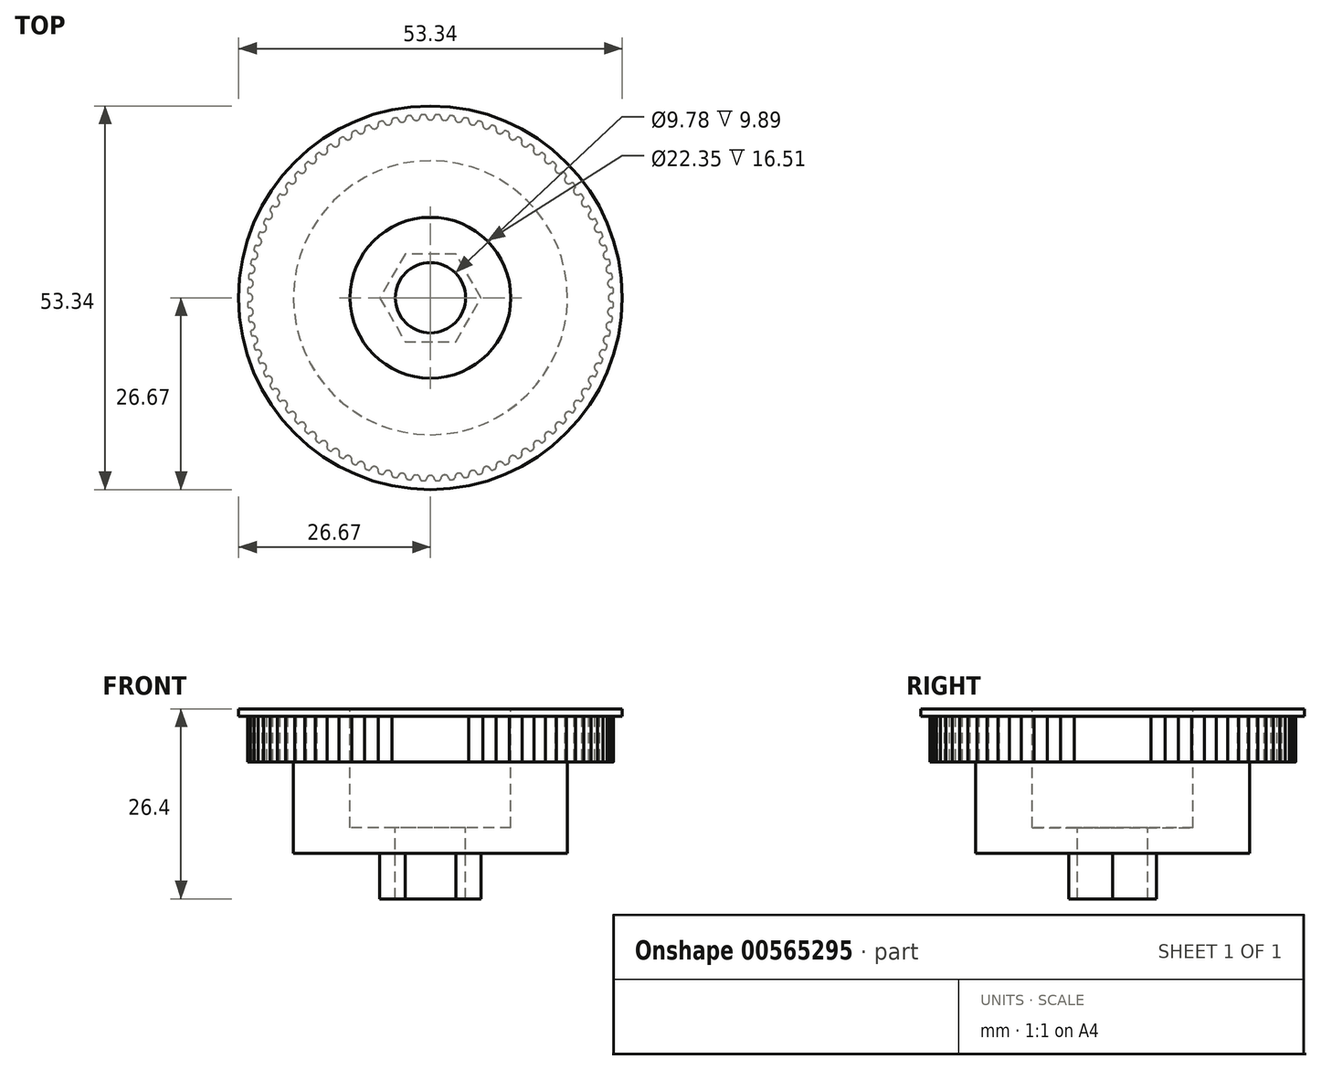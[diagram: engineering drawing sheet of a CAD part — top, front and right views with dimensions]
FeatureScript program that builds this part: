
annotation { "Feature Type Name" : "Feature", "Feature Type Description" : "" }
export const myFeature = defineFeature(function(context is Context, id is Id, definition is map)
    precondition{}
    {
        {
            var Q0;
            Q0=qCreatedBy(makeId("Top.planeOp"),FACE);
            var sketch = newSketch(context, id + "F0", { "sketchPlane" : qUnion([Q0])});
            skArc(sketch, "E0", {"start": v(0, 24.71) * mm, "mid": v(0.3, 24.8) * mm, "end": v(0.5, 25.03) * mm});
            skArc(sketch, "E1", {"start": v(0.5, 25.03) * mm, "mid": v(0.54, 25.14) * mm, "end": v(0.58, 25.25) * mm});
            skArc(sketch, "E2", {"start": v(1.46, 25) * mm, "mid": v(1.65, 24.75) * mm, "end": v(1.94, 24.64) * mm});
            skArc(sketch, "E3", {"start": v(1.4, 25.22) * mm, "mid": v(1.43, 25.1) * mm, "end": v(1.46, 25) * mm});
            skArc(sketch, "E4.trimOffspring", {"start": v(1.17, 25.44) * mm, "mid": v(1, 25.44) * mm, "end": v(0.83, 25.45) * mm});
            skPoint(sketch, "E5.visualSharp", {"position": v(0.6, 25.46) * mm});
            skArc(sketch, "E5.filletArc", {"start": v(0.83, 25.45) * mm, "mid": v(0.67, 25.4) * mm, "end": v(0.58, 25.25) * mm});
            skPoint(sketch, "E6.visualSharp", {"position": v(1.4, 25.42) * mm});
            skArc(sketch, "E6.filletArc", {"start": v(1.4, 25.22) * mm, "mid": v(1.33, 25.37) * mm, "end": v(1.17, 25.44) * mm});
            skArc(sketch, "E7.1.0", {"start": v(-1.94, 24.64) * mm, "mid": v(-1.65, 24.75) * mm, "end": v(-1.46, 25) * mm});
            skArc(sketch, "E7.1.1", {"start": v(-1.46, 25) * mm, "mid": v(-1.43, 25.1) * mm, "end": v(-1.4, 25.22) * mm});
            skArc(sketch, "E7.1.2", {"start": v(-1.17, 25.44) * mm, "mid": v(-1.33, 25.37) * mm, "end": v(-1.4, 25.22) * mm});
            skArc(sketch, "E7.1.3", {"start": v(-0.83, 25.45) * mm, "mid": v(-1, 25.44) * mm, "end": v(-1.17, 25.44) * mm});
            skArc(sketch, "E7.1.4", {"start": v(-0.58, 25.25) * mm, "mid": v(-0.67, 25.4) * mm, "end": v(-0.83, 25.45) * mm});
            skArc(sketch, "E7.1.5", {"start": v(-0.58, 25.25) * mm, "mid": v(-0.54, 25.14) * mm, "end": v(-0.5, 25.03) * mm});
            skArc(sketch, "E7.1.6", {"start": v(-0.5, 25.03) * mm, "mid": v(-0.3, 24.8) * mm, "end": v(0, 24.71) * mm});
            skArc(sketch, "E7.2.0", {"start": v(-3.87, 24.4) * mm, "mid": v(-3.59, 24.54) * mm, "end": v(-3.42, 24.8) * mm});
            skArc(sketch, "E7.2.1", {"start": v(-3.42, 24.8) * mm, "mid": v(-3.4, 24.91) * mm, "end": v(-3.38, 25.03) * mm});
            skArc(sketch, "E7.2.2", {"start": v(-3.16, 25.27) * mm, "mid": v(-3.31, 25.19) * mm, "end": v(-3.38, 25.03) * mm});
            skArc(sketch, "E7.2.3", {"start": v(-2.83, 25.3) * mm, "mid": v(-3, 25.29) * mm, "end": v(-3.16, 25.27) * mm});
            skArc(sketch, "E7.2.4", {"start": v(-2.55, 25.13) * mm, "mid": v(-2.66, 25.27) * mm, "end": v(-2.83, 25.3) * mm});
            skArc(sketch, "E7.2.5", {"start": v(-2.55, 25.13) * mm, "mid": v(-2.52, 25.02) * mm, "end": v(-2.46, 24.91) * mm});
            skArc(sketch, "E7.2.6", {"start": v(-2.46, 24.91) * mm, "mid": v(-2.24, 24.7) * mm, "end": v(-1.94, 24.64) * mm});
            skArc(sketch, "E7.3.0", {"start": v(-5.77, 24.03) * mm, "mid": v(-5.5, 24.18) * mm, "end": v(-5.36, 24.46) * mm});
            skArc(sketch, "E7.3.1", {"start": v(-5.36, 24.46) * mm, "mid": v(-5.34, 24.57) * mm, "end": v(-5.33, 24.69) * mm});
            skArc(sketch, "E7.3.2", {"start": v(-5.13, 24.94) * mm, "mid": v(-5.28, 24.85) * mm, "end": v(-5.33, 24.69) * mm});
            skArc(sketch, "E7.3.3", {"start": v(-4.8, 25) * mm, "mid": v(-4.97, 24.97) * mm, "end": v(-5.13, 24.94) * mm});
            skArc(sketch, "E7.3.4", {"start": v(-4.52, 24.85) * mm, "mid": v(-4.63, 24.98) * mm, "end": v(-4.8, 25) * mm});
            skArc(sketch, "E7.3.5", {"start": v(-4.52, 24.85) * mm, "mid": v(-4.47, 24.74) * mm, "end": v(-4.41, 24.64) * mm});
            skArc(sketch, "E7.3.6", {"start": v(-4.41, 24.64) * mm, "mid": v(-4.17, 24.45) * mm, "end": v(-3.87, 24.4) * mm});
            skArc(sketch, "E7.4.0", {"start": v(-7.64, 23.5) * mm, "mid": v(-7.38, 23.68) * mm, "end": v(-7.26, 23.96) * mm});
            skArc(sketch, "E7.4.1", {"start": v(-7.26, 23.96) * mm, "mid": v(-7.25, 24.08) * mm, "end": v(-7.26, 24.2) * mm});
            skArc(sketch, "E7.4.2", {"start": v(-7.07, 24.46) * mm, "mid": v(-7.21, 24.36) * mm, "end": v(-7.26, 24.2) * mm});
            skArc(sketch, "E7.4.3", {"start": v(-6.75, 24.55) * mm, "mid": v(-6.91, 24.5) * mm, "end": v(-7.07, 24.46) * mm});
            skArc(sketch, "E7.4.4", {"start": v(-6.45, 24.42) * mm, "mid": v(-6.58, 24.54) * mm, "end": v(-6.75, 24.55) * mm});
            skArc(sketch, "E7.4.5", {"start": v(-6.45, 24.42) * mm, "mid": v(-6.4, 24.32) * mm, "end": v(-6.33, 24.22) * mm});
            skArc(sketch, "E7.4.6", {"start": v(-6.33, 24.22) * mm, "mid": v(-6.08, 24.05) * mm, "end": v(-5.77, 24.03) * mm});
            skArc(sketch, "E7.5.0", {"start": v(-9.46, 22.83) * mm, "mid": v(-9.22, 23.03) * mm, "end": v(-9.12, 23.32) * mm});
            skArc(sketch, "E7.5.1", {"start": v(-9.12, 23.32) * mm, "mid": v(-9.12, 23.43) * mm, "end": v(-9.13, 23.55) * mm});
            skArc(sketch, "E7.5.2", {"start": v(-8.97, 23.83) * mm, "mid": v(-9.1, 23.72) * mm, "end": v(-9.13, 23.55) * mm});
            skArc(sketch, "E7.5.3", {"start": v(-8.66, 23.95) * mm, "mid": v(-8.81, 23.89) * mm, "end": v(-8.97, 23.83) * mm});
            skArc(sketch, "E7.5.4", {"start": v(-8.35, 23.84) * mm, "mid": v(-8.48, 23.95) * mm, "end": v(-8.66, 23.95) * mm});
            skArc(sketch, "E7.5.5", {"start": v(-8.35, 23.84) * mm, "mid": v(-8.29, 23.74) * mm, "end": v(-8.21, 23.65) * mm});
            skArc(sketch, "E7.5.6", {"start": v(-8.21, 23.65) * mm, "mid": v(-7.95, 23.5) * mm, "end": v(-7.64, 23.5) * mm});
            skArc(sketch, "E7.6.0", {"start": v(-11.22, 22.02) * mm, "mid": v(-11, 22.23) * mm, "end": v(-10.92, 22.53) * mm});
            skArc(sketch, "E7.6.1", {"start": v(-10.92, 22.53) * mm, "mid": v(-10.93, 22.65) * mm, "end": v(-10.95, 22.76) * mm});
            skArc(sketch, "E7.6.2", {"start": v(-10.81, 23.05) * mm, "mid": v(-10.93, 22.93) * mm, "end": v(-10.95, 22.76) * mm});
            skArc(sketch, "E7.6.3", {"start": v(-10.5, 23.2) * mm, "mid": v(-10.66, 23.12) * mm, "end": v(-10.81, 23.05) * mm});
            skArc(sketch, "E7.6.4", {"start": v(-10.2, 23.1) * mm, "mid": v(-10.34, 23.2) * mm, "end": v(-10.5, 23.2) * mm});
            skArc(sketch, "E7.6.5", {"start": v(-10.2, 23.1) * mm, "mid": v(-10.12, 23.02) * mm, "end": v(-10.04, 22.93) * mm});
            skArc(sketch, "E7.6.6", {"start": v(-10.04, 22.93) * mm, "mid": v(-9.76, 22.8) * mm, "end": v(-9.46, 22.83) * mm});
            skArc(sketch, "E7.7.0", {"start": v(-12.91, 21.07) * mm, "mid": v(-12.7, 21.3) * mm, "end": v(-12.65, 21.6) * mm});
            skArc(sketch, "E7.7.1", {"start": v(-12.65, 21.6) * mm, "mid": v(-12.67, 21.72) * mm, "end": v(-12.7, 21.83) * mm});
            skArc(sketch, "E7.7.2", {"start": v(-12.59, 22.13) * mm, "mid": v(-12.7, 22) * mm, "end": v(-12.7, 21.83) * mm});
            skArc(sketch, "E7.7.3", {"start": v(-12.3, 22.3) * mm, "mid": v(-12.44, 22.22) * mm, "end": v(-12.59, 22.13) * mm});
            skArc(sketch, "E7.7.4", {"start": v(-11.98, 22.24) * mm, "mid": v(-12.12, 22.33) * mm, "end": v(-12.3, 22.3) * mm});
            skArc(sketch, "E7.7.5", {"start": v(-11.98, 22.24) * mm, "mid": v(-11.9, 22.15) * mm, "end": v(-11.81, 22.08) * mm});
            skArc(sketch, "E7.7.6", {"start": v(-11.81, 22.08) * mm, "mid": v(-11.52, 21.96) * mm, "end": v(-11.22, 22.02) * mm});
            skArc(sketch, "E7.8.0", {"start": v(-14.53, 20) * mm, "mid": v(-14.34, 20.24) * mm, "end": v(-14.3, 20.54) * mm});
            skArc(sketch, "E7.8.1", {"start": v(-14.3, 20.54) * mm, "mid": v(-14.34, 20.66) * mm, "end": v(-14.38, 20.77) * mm});
            skArc(sketch, "E7.8.2", {"start": v(-14.29, 21.08) * mm, "mid": v(-14.39, 20.94) * mm, "end": v(-14.38, 20.77) * mm});
            skArc(sketch, "E7.8.3", {"start": v(-14, 21.26) * mm, "mid": v(-14.15, 21.17) * mm, "end": v(-14.29, 21.08) * mm});
            skArc(sketch, "E7.8.4", {"start": v(-13.68, 21.23) * mm, "mid": v(-13.84, 21.3) * mm, "end": v(-14, 21.26) * mm});
            skArc(sketch, "E7.8.5", {"start": v(-13.68, 21.23) * mm, "mid": v(-13.6, 21.15) * mm, "end": v(-13.5, 21.08) * mm});
            skArc(sketch, "E7.8.6", {"start": v(-13.5, 21.08) * mm, "mid": v(-13.21, 21) * mm, "end": v(-12.91, 21.07) * mm});
            skArc(sketch, "E7.9.0", {"start": v(-16.05, 18.8) * mm, "mid": v(-15.88, 19.05) * mm, "end": v(-15.88, 19.36) * mm});
            skArc(sketch, "E7.9.1", {"start": v(-15.88, 19.36) * mm, "mid": v(-15.91, 19.47) * mm, "end": v(-15.96, 19.57) * mm});
            skArc(sketch, "E7.9.2", {"start": v(-15.9, 19.9) * mm, "mid": v(-15.99, 19.75) * mm, "end": v(-15.96, 19.57) * mm});
            skArc(sketch, "E7.9.3", {"start": v(-15.63, 20.1) * mm, "mid": v(-15.76, 20) * mm, "end": v(-15.9, 19.9) * mm});
            skArc(sketch, "E7.9.4", {"start": v(-15.3, 20.09) * mm, "mid": v(-15.47, 20.15) * mm, "end": v(-15.63, 20.1) * mm});
            skArc(sketch, "E7.9.5", {"start": v(-15.3, 20.09) * mm, "mid": v(-15.22, 20.02) * mm, "end": v(-15.12, 19.96) * mm});
            skArc(sketch, "E7.9.6", {"start": v(-15.12, 19.96) * mm, "mid": v(-14.82, 19.89) * mm, "end": v(-14.53, 20) * mm});
            skArc(sketch, "E7.10.0", {"start": v(-17.48, 17.48) * mm, "mid": v(-17.33, 17.75) * mm, "end": v(-17.35, 18.05) * mm});
            skArc(sketch, "E7.10.1", {"start": v(-17.35, 18.05) * mm, "mid": v(-17.4, 18.16) * mm, "end": v(-17.45, 18.26) * mm});
            skArc(sketch, "E7.10.2", {"start": v(-17.4, 18.58) * mm, "mid": v(-17.49, 18.43) * mm, "end": v(-17.45, 18.26) * mm});
            skArc(sketch, "E7.10.3", {"start": v(-17.16, 18.81) * mm, "mid": v(-17.28, 18.7) * mm, "end": v(-17.4, 18.58) * mm});
            skArc(sketch, "E7.10.4", {"start": v(-16.84, 18.83) * mm, "mid": v(-17, 18.88) * mm, "end": v(-17.16, 18.81) * mm});
            skArc(sketch, "E7.10.5", {"start": v(-16.84, 18.83) * mm, "mid": v(-16.74, 18.76) * mm, "end": v(-16.64, 18.7) * mm});
            skArc(sketch, "E7.10.6", {"start": v(-16.64, 18.7) * mm, "mid": v(-16.33, 18.67) * mm, "end": v(-16.05, 18.8) * mm});
            skArc(sketch, "E7.11.0", {"start": v(-18.8, 16.05) * mm, "mid": v(-18.67, 16.33) * mm, "end": v(-18.7, 16.64) * mm});
            skArc(sketch, "E7.11.1", {"start": v(-18.7, 16.64) * mm, "mid": v(-18.76, 16.74) * mm, "end": v(-18.83, 16.84) * mm});
            skArc(sketch, "E7.11.2", {"start": v(-18.81, 17.16) * mm, "mid": v(-18.88, 17) * mm, "end": v(-18.83, 16.84) * mm});
            skArc(sketch, "E7.11.3", {"start": v(-18.58, 17.4) * mm, "mid": v(-18.7, 17.28) * mm, "end": v(-18.81, 17.16) * mm});
            skArc(sketch, "E7.11.4", {"start": v(-18.26, 17.45) * mm, "mid": v(-18.43, 17.49) * mm, "end": v(-18.58, 17.4) * mm});
            skArc(sketch, "E7.11.5", {"start": v(-18.26, 17.45) * mm, "mid": v(-18.16, 17.4) * mm, "end": v(-18.05, 17.35) * mm});
            skArc(sketch, "E7.11.6", {"start": v(-18.05, 17.35) * mm, "mid": v(-17.75, 17.33) * mm, "end": v(-17.48, 17.48) * mm});
            skArc(sketch, "E7.12.0", {"start": v(-20, 14.53) * mm, "mid": v(-19.89, 14.82) * mm, "end": v(-19.96, 15.12) * mm});
            skArc(sketch, "E7.12.1", {"start": v(-19.96, 15.12) * mm, "mid": v(-20.02, 15.22) * mm, "end": v(-20.09, 15.3) * mm});
            skArc(sketch, "E7.12.2", {"start": v(-20.1, 15.63) * mm, "mid": v(-20.15, 15.47) * mm, "end": v(-20.09, 15.3) * mm});
            skArc(sketch, "E7.12.3", {"start": v(-19.9, 15.9) * mm, "mid": v(-20, 15.76) * mm, "end": v(-20.1, 15.63) * mm});
            skArc(sketch, "E7.12.4", {"start": v(-19.57, 15.96) * mm, "mid": v(-19.75, 15.99) * mm, "end": v(-19.9, 15.9) * mm});
            skArc(sketch, "E7.12.5", {"start": v(-19.57, 15.96) * mm, "mid": v(-19.47, 15.91) * mm, "end": v(-19.36, 15.88) * mm});
            skArc(sketch, "E7.12.6", {"start": v(-19.36, 15.88) * mm, "mid": v(-19.05, 15.88) * mm, "end": v(-18.8, 16.05) * mm});
            skArc(sketch, "E7.13.0", {"start": v(-21.07, 12.91) * mm, "mid": v(-21, 13.21) * mm, "end": v(-21.08, 13.5) * mm});
            skArc(sketch, "E7.13.1", {"start": v(-21.08, 13.5) * mm, "mid": v(-21.15, 13.6) * mm, "end": v(-21.23, 13.68) * mm});
            skArc(sketch, "E7.13.2", {"start": v(-21.26, 14) * mm, "mid": v(-21.3, 13.84) * mm, "end": v(-21.23, 13.68) * mm});
            skArc(sketch, "E7.13.3", {"start": v(-21.08, 14.29) * mm, "mid": v(-21.17, 14.15) * mm, "end": v(-21.26, 14) * mm});
            skArc(sketch, "E7.13.4", {"start": v(-20.77, 14.38) * mm, "mid": v(-20.94, 14.39) * mm, "end": v(-21.08, 14.29) * mm});
            skArc(sketch, "E7.13.5", {"start": v(-20.77, 14.38) * mm, "mid": v(-20.66, 14.34) * mm, "end": v(-20.54, 14.3) * mm});
            skArc(sketch, "E7.13.6", {"start": v(-20.54, 14.3) * mm, "mid": v(-20.24, 14.34) * mm, "end": v(-20, 14.53) * mm});
            skArc(sketch, "E7.14.0", {"start": v(-22.02, 11.22) * mm, "mid": v(-21.96, 11.52) * mm, "end": v(-22.08, 11.81) * mm});
            skArc(sketch, "E7.14.1", {"start": v(-22.08, 11.81) * mm, "mid": v(-22.15, 11.9) * mm, "end": v(-22.24, 11.98) * mm});
            skArc(sketch, "E7.14.2", {"start": v(-22.3, 12.3) * mm, "mid": v(-22.33, 12.12) * mm, "end": v(-22.24, 11.98) * mm});
            skArc(sketch, "E7.14.3", {"start": v(-22.13, 12.59) * mm, "mid": v(-22.22, 12.44) * mm, "end": v(-22.3, 12.3) * mm});
            skArc(sketch, "E7.14.4", {"start": v(-21.83, 12.7) * mm, "mid": v(-22, 12.7) * mm, "end": v(-22.13, 12.59) * mm});
            skArc(sketch, "E7.14.5", {"start": v(-21.83, 12.7) * mm, "mid": v(-21.72, 12.67) * mm, "end": v(-21.6, 12.65) * mm});
            skArc(sketch, "E7.14.6", {"start": v(-21.6, 12.65) * mm, "mid": v(-21.3, 12.7) * mm, "end": v(-21.07, 12.91) * mm});
            skArc(sketch, "E7.15.0", {"start": v(-22.83, 9.46) * mm, "mid": v(-22.8, 9.76) * mm, "end": v(-22.93, 10.04) * mm});
            skArc(sketch, "E7.15.1", {"start": v(-22.93, 10.04) * mm, "mid": v(-23.02, 10.12) * mm, "end": v(-23.1, 10.2) * mm});
            skArc(sketch, "E7.15.2", {"start": v(-23.2, 10.5) * mm, "mid": v(-23.2, 10.34) * mm, "end": v(-23.1, 10.2) * mm});
            skArc(sketch, "E7.15.3", {"start": v(-23.05, 10.81) * mm, "mid": v(-23.12, 10.66) * mm, "end": v(-23.2, 10.5) * mm});
            skArc(sketch, "E7.15.4", {"start": v(-22.76, 10.95) * mm, "mid": v(-22.93, 10.93) * mm, "end": v(-23.05, 10.81) * mm});
            skArc(sketch, "E7.15.5", {"start": v(-22.76, 10.95) * mm, "mid": v(-22.65, 10.93) * mm, "end": v(-22.53, 10.92) * mm});
            skArc(sketch, "E7.15.6", {"start": v(-22.53, 10.92) * mm, "mid": v(-22.23, 11) * mm, "end": v(-22.02, 11.22) * mm});
            skArc(sketch, "E7.16.0", {"start": v(-23.5, 7.64) * mm, "mid": v(-23.5, 7.95) * mm, "end": v(-23.65, 8.21) * mm});
            skArc(sketch, "E7.16.1", {"start": v(-23.65, 8.21) * mm, "mid": v(-23.74, 8.29) * mm, "end": v(-23.84, 8.35) * mm});
            skArc(sketch, "E7.16.2", {"start": v(-23.95, 8.66) * mm, "mid": v(-23.95, 8.48) * mm, "end": v(-23.84, 8.35) * mm});
            skArc(sketch, "E7.16.3", {"start": v(-23.83, 8.97) * mm, "mid": v(-23.89, 8.81) * mm, "end": v(-23.95, 8.66) * mm});
            skArc(sketch, "E7.16.4", {"start": v(-23.55, 9.13) * mm, "mid": v(-23.72, 9.1) * mm, "end": v(-23.83, 8.97) * mm});
            skArc(sketch, "E7.16.5", {"start": v(-23.55, 9.13) * mm, "mid": v(-23.43, 9.12) * mm, "end": v(-23.32, 9.12) * mm});
            skArc(sketch, "E7.16.6", {"start": v(-23.32, 9.12) * mm, "mid": v(-23.03, 9.22) * mm, "end": v(-22.83, 9.46) * mm});
            skArc(sketch, "E7.17.0", {"start": v(-24.03, 5.77) * mm, "mid": v(-24.05, 6.08) * mm, "end": v(-24.22, 6.33) * mm});
            skArc(sketch, "E7.17.1", {"start": v(-24.22, 6.33) * mm, "mid": v(-24.32, 6.4) * mm, "end": v(-24.42, 6.45) * mm});
            skArc(sketch, "E7.17.2", {"start": v(-24.55, 6.75) * mm, "mid": v(-24.54, 6.58) * mm, "end": v(-24.42, 6.45) * mm});
            skArc(sketch, "E7.17.3", {"start": v(-24.46, 7.07) * mm, "mid": v(-24.5, 6.91) * mm, "end": v(-24.55, 6.75) * mm});
            skArc(sketch, "E7.17.4", {"start": v(-24.2, 7.26) * mm, "mid": v(-24.36, 7.21) * mm, "end": v(-24.46, 7.07) * mm});
            skArc(sketch, "E7.17.5", {"start": v(-24.2, 7.26) * mm, "mid": v(-24.08, 7.25) * mm, "end": v(-23.96, 7.26) * mm});
            skArc(sketch, "E7.17.6", {"start": v(-23.96, 7.26) * mm, "mid": v(-23.68, 7.38) * mm, "end": v(-23.5, 7.64) * mm});
            skArc(sketch, "E7.18.0", {"start": v(-24.4, 3.87) * mm, "mid": v(-24.45, 4.17) * mm, "end": v(-24.64, 4.41) * mm});
            skArc(sketch, "E7.18.1", {"start": v(-24.64, 4.41) * mm, "mid": v(-24.74, 4.47) * mm, "end": v(-24.85, 4.52) * mm});
            skArc(sketch, "E7.18.2", {"start": v(-25, 4.8) * mm, "mid": v(-24.98, 4.63) * mm, "end": v(-24.85, 4.52) * mm});
            skArc(sketch, "E7.18.3", {"start": v(-24.94, 5.13) * mm, "mid": v(-24.97, 4.97) * mm, "end": v(-25, 4.8) * mm});
            skArc(sketch, "E7.18.4", {"start": v(-24.69, 5.33) * mm, "mid": v(-24.85, 5.28) * mm, "end": v(-24.94, 5.13) * mm});
            skArc(sketch, "E7.18.5", {"start": v(-24.69, 5.33) * mm, "mid": v(-24.57, 5.34) * mm, "end": v(-24.46, 5.36) * mm});
            skArc(sketch, "E7.18.6", {"start": v(-24.46, 5.36) * mm, "mid": v(-24.18, 5.5) * mm, "end": v(-24.03, 5.77) * mm});
            skArc(sketch, "E7.19.0", {"start": v(-24.64, 1.94) * mm, "mid": v(-24.7, 2.24) * mm, "end": v(-24.91, 2.46) * mm});
            skArc(sketch, "E7.19.1", {"start": v(-24.91, 2.46) * mm, "mid": v(-25.02, 2.52) * mm, "end": v(-25.13, 2.55) * mm});
            skArc(sketch, "E7.19.2", {"start": v(-25.3, 2.83) * mm, "mid": v(-25.27, 2.66) * mm, "end": v(-25.13, 2.55) * mm});
            skArc(sketch, "E7.19.3", {"start": v(-25.27, 3.16) * mm, "mid": v(-25.29, 3) * mm, "end": v(-25.3, 2.83) * mm});
            skArc(sketch, "E7.19.4", {"start": v(-25.03, 3.38) * mm, "mid": v(-25.19, 3.31) * mm, "end": v(-25.27, 3.16) * mm});
            skArc(sketch, "E7.19.5", {"start": v(-25.03, 3.38) * mm, "mid": v(-24.91, 3.4) * mm, "end": v(-24.8, 3.42) * mm});
            skArc(sketch, "E7.19.6", {"start": v(-24.8, 3.42) * mm, "mid": v(-24.54, 3.59) * mm, "end": v(-24.4, 3.87) * mm});
            skArc(sketch, "E7.20.0", {"start": v(-24.71, 0) * mm, "mid": v(-24.8, 0.3) * mm, "end": v(-25.03, 0.5) * mm});
            skArc(sketch, "E7.20.1", {"start": v(-25.03, 0.5) * mm, "mid": v(-25.14, 0.54) * mm, "end": v(-25.25, 0.58) * mm});
            skArc(sketch, "E7.20.2", {"start": v(-25.45, 0.83) * mm, "mid": v(-25.4, 0.67) * mm, "end": v(-25.25, 0.58) * mm});
            skArc(sketch, "E7.20.3", {"start": v(-25.44, 1.17) * mm, "mid": v(-25.44, 1) * mm, "end": v(-25.45, 0.83) * mm});
            skArc(sketch, "E7.20.4", {"start": v(-25.22, 1.4) * mm, "mid": v(-25.37, 1.33) * mm, "end": v(-25.44, 1.17) * mm});
            skArc(sketch, "E7.20.5", {"start": v(-25.22, 1.4) * mm, "mid": v(-25.1, 1.43) * mm, "end": v(-25, 1.46) * mm});
            skArc(sketch, "E7.20.6", {"start": v(-25, 1.46) * mm, "mid": v(-24.75, 1.65) * mm, "end": v(-24.64, 1.94) * mm});
            skArc(sketch, "E7.21.0", {"start": v(-24.64, -1.94) * mm, "mid": v(-24.75, -1.65) * mm, "end": v(-25, -1.46) * mm});
            skArc(sketch, "E7.21.1", {"start": v(-25, -1.46) * mm, "mid": v(-25.1, -1.43) * mm, "end": v(-25.22, -1.4) * mm});
            skArc(sketch, "E7.21.2", {"start": v(-25.44, -1.17) * mm, "mid": v(-25.37, -1.33) * mm, "end": v(-25.22, -1.4) * mm});
            skArc(sketch, "E7.21.3", {"start": v(-25.45, -0.83) * mm, "mid": v(-25.44, -1) * mm, "end": v(-25.44, -1.17) * mm});
            skArc(sketch, "E7.21.4", {"start": v(-25.25, -0.58) * mm, "mid": v(-25.4, -0.67) * mm, "end": v(-25.45, -0.83) * mm});
            skArc(sketch, "E7.21.5", {"start": v(-25.25, -0.58) * mm, "mid": v(-25.14, -0.54) * mm, "end": v(-25.03, -0.5) * mm});
            skArc(sketch, "E7.21.6", {"start": v(-25.03, -0.5) * mm, "mid": v(-24.8, -0.3) * mm, "end": v(-24.71, 0) * mm});
            skArc(sketch, "E7.22.0", {"start": v(-24.4, -3.87) * mm, "mid": v(-24.54, -3.59) * mm, "end": v(-24.8, -3.42) * mm});
            skArc(sketch, "E7.22.1", {"start": v(-24.8, -3.42) * mm, "mid": v(-24.91, -3.4) * mm, "end": v(-25.03, -3.38) * mm});
            skArc(sketch, "E7.22.2", {"start": v(-25.27, -3.16) * mm, "mid": v(-25.19, -3.31) * mm, "end": v(-25.03, -3.38) * mm});
            skArc(sketch, "E7.22.3", {"start": v(-25.3, -2.83) * mm, "mid": v(-25.29, -3) * mm, "end": v(-25.27, -3.16) * mm});
            skArc(sketch, "E7.22.4", {"start": v(-25.13, -2.55) * mm, "mid": v(-25.27, -2.66) * mm, "end": v(-25.3, -2.83) * mm});
            skArc(sketch, "E7.22.5", {"start": v(-25.13, -2.55) * mm, "mid": v(-25.02, -2.52) * mm, "end": v(-24.91, -2.46) * mm});
            skArc(sketch, "E7.22.6", {"start": v(-24.91, -2.46) * mm, "mid": v(-24.7, -2.24) * mm, "end": v(-24.64, -1.94) * mm});
            skArc(sketch, "E7.23.0", {"start": v(-24.03, -5.77) * mm, "mid": v(-24.18, -5.5) * mm, "end": v(-24.46, -5.36) * mm});
            skArc(sketch, "E7.23.1", {"start": v(-24.46, -5.36) * mm, "mid": v(-24.57, -5.34) * mm, "end": v(-24.69, -5.33) * mm});
            skArc(sketch, "E7.23.2", {"start": v(-24.94, -5.13) * mm, "mid": v(-24.85, -5.28) * mm, "end": v(-24.69, -5.33) * mm});
            skArc(sketch, "E7.23.3", {"start": v(-25, -4.8) * mm, "mid": v(-24.97, -4.97) * mm, "end": v(-24.94, -5.13) * mm});
            skArc(sketch, "E7.23.4", {"start": v(-24.85, -4.52) * mm, "mid": v(-24.98, -4.63) * mm, "end": v(-25, -4.8) * mm});
            skArc(sketch, "E7.23.5", {"start": v(-24.85, -4.52) * mm, "mid": v(-24.74, -4.47) * mm, "end": v(-24.64, -4.41) * mm});
            skArc(sketch, "E7.23.6", {"start": v(-24.64, -4.41) * mm, "mid": v(-24.45, -4.17) * mm, "end": v(-24.4, -3.87) * mm});
            skArc(sketch, "E7.24.0", {"start": v(-23.5, -7.64) * mm, "mid": v(-23.68, -7.38) * mm, "end": v(-23.96, -7.26) * mm});
            skArc(sketch, "E7.24.1", {"start": v(-23.96, -7.26) * mm, "mid": v(-24.08, -7.25) * mm, "end": v(-24.2, -7.26) * mm});
            skArc(sketch, "E7.24.2", {"start": v(-24.46, -7.07) * mm, "mid": v(-24.36, -7.21) * mm, "end": v(-24.2, -7.26) * mm});
            skArc(sketch, "E7.24.3", {"start": v(-24.55, -6.75) * mm, "mid": v(-24.5, -6.91) * mm, "end": v(-24.46, -7.07) * mm});
            skArc(sketch, "E7.24.4", {"start": v(-24.42, -6.45) * mm, "mid": v(-24.54, -6.58) * mm, "end": v(-24.55, -6.75) * mm});
            skArc(sketch, "E7.24.5", {"start": v(-24.42, -6.45) * mm, "mid": v(-24.32, -6.4) * mm, "end": v(-24.22, -6.33) * mm});
            skArc(sketch, "E7.24.6", {"start": v(-24.22, -6.33) * mm, "mid": v(-24.05, -6.08) * mm, "end": v(-24.03, -5.77) * mm});
            skArc(sketch, "E7.25.0", {"start": v(-22.83, -9.46) * mm, "mid": v(-23.03, -9.22) * mm, "end": v(-23.32, -9.12) * mm});
            skArc(sketch, "E7.25.1", {"start": v(-23.32, -9.12) * mm, "mid": v(-23.43, -9.12) * mm, "end": v(-23.55, -9.13) * mm});
            skArc(sketch, "E7.25.2", {"start": v(-23.83, -8.97) * mm, "mid": v(-23.72, -9.1) * mm, "end": v(-23.55, -9.13) * mm});
            skArc(sketch, "E7.25.3", {"start": v(-23.95, -8.66) * mm, "mid": v(-23.89, -8.81) * mm, "end": v(-23.83, -8.97) * mm});
            skArc(sketch, "E7.25.4", {"start": v(-23.84, -8.35) * mm, "mid": v(-23.95, -8.48) * mm, "end": v(-23.95, -8.66) * mm});
            skArc(sketch, "E7.25.5", {"start": v(-23.84, -8.35) * mm, "mid": v(-23.74, -8.29) * mm, "end": v(-23.65, -8.21) * mm});
            skArc(sketch, "E7.25.6", {"start": v(-23.65, -8.21) * mm, "mid": v(-23.5, -7.95) * mm, "end": v(-23.5, -7.64) * mm});
            skArc(sketch, "E7.26.0", {"start": v(-22.02, -11.22) * mm, "mid": v(-22.23, -11) * mm, "end": v(-22.53, -10.92) * mm});
            skArc(sketch, "E7.26.1", {"start": v(-22.53, -10.92) * mm, "mid": v(-22.65, -10.93) * mm, "end": v(-22.76, -10.95) * mm});
            skArc(sketch, "E7.26.2", {"start": v(-23.05, -10.81) * mm, "mid": v(-22.93, -10.93) * mm, "end": v(-22.76, -10.95) * mm});
            skArc(sketch, "E7.26.3", {"start": v(-23.2, -10.5) * mm, "mid": v(-23.12, -10.66) * mm, "end": v(-23.05, -10.81) * mm});
            skArc(sketch, "E7.26.4", {"start": v(-23.1, -10.2) * mm, "mid": v(-23.2, -10.34) * mm, "end": v(-23.2, -10.5) * mm});
            skArc(sketch, "E7.26.5", {"start": v(-23.1, -10.2) * mm, "mid": v(-23.02, -10.12) * mm, "end": v(-22.93, -10.04) * mm});
            skArc(sketch, "E7.26.6", {"start": v(-22.93, -10.04) * mm, "mid": v(-22.8, -9.76) * mm, "end": v(-22.83, -9.46) * mm});
            skArc(sketch, "E7.27.0", {"start": v(-21.07, -12.91) * mm, "mid": v(-21.3, -12.7) * mm, "end": v(-21.6, -12.65) * mm});
            skArc(sketch, "E7.27.1", {"start": v(-21.6, -12.65) * mm, "mid": v(-21.72, -12.67) * mm, "end": v(-21.83, -12.7) * mm});
            skArc(sketch, "E7.27.2", {"start": v(-22.13, -12.59) * mm, "mid": v(-22, -12.7) * mm, "end": v(-21.83, -12.7) * mm});
            skArc(sketch, "E7.27.3", {"start": v(-22.3, -12.3) * mm, "mid": v(-22.22, -12.44) * mm, "end": v(-22.13, -12.59) * mm});
            skArc(sketch, "E7.27.4", {"start": v(-22.24, -11.98) * mm, "mid": v(-22.33, -12.12) * mm, "end": v(-22.3, -12.3) * mm});
            skArc(sketch, "E7.27.5", {"start": v(-22.24, -11.98) * mm, "mid": v(-22.15, -11.9) * mm, "end": v(-22.08, -11.81) * mm});
            skArc(sketch, "E7.27.6", {"start": v(-22.08, -11.81) * mm, "mid": v(-21.96, -11.52) * mm, "end": v(-22.02, -11.22) * mm});
            skArc(sketch, "E7.28.0", {"start": v(-20, -14.53) * mm, "mid": v(-20.24, -14.34) * mm, "end": v(-20.54, -14.3) * mm});
            skArc(sketch, "E7.28.1", {"start": v(-20.54, -14.3) * mm, "mid": v(-20.66, -14.34) * mm, "end": v(-20.77, -14.38) * mm});
            skArc(sketch, "E7.28.2", {"start": v(-21.08, -14.29) * mm, "mid": v(-20.94, -14.39) * mm, "end": v(-20.77, -14.38) * mm});
            skArc(sketch, "E7.28.3", {"start": v(-21.26, -14) * mm, "mid": v(-21.17, -14.15) * mm, "end": v(-21.08, -14.29) * mm});
            skArc(sketch, "E7.28.4", {"start": v(-21.23, -13.68) * mm, "mid": v(-21.3, -13.84) * mm, "end": v(-21.26, -14) * mm});
            skArc(sketch, "E7.28.5", {"start": v(-21.23, -13.68) * mm, "mid": v(-21.15, -13.6) * mm, "end": v(-21.08, -13.5) * mm});
            skArc(sketch, "E7.28.6", {"start": v(-21.08, -13.5) * mm, "mid": v(-21, -13.21) * mm, "end": v(-21.07, -12.91) * mm});
            skArc(sketch, "E7.29.0", {"start": v(-18.8, -16.05) * mm, "mid": v(-19.05, -15.88) * mm, "end": v(-19.36, -15.88) * mm});
            skArc(sketch, "E7.29.1", {"start": v(-19.36, -15.88) * mm, "mid": v(-19.47, -15.91) * mm, "end": v(-19.57, -15.96) * mm});
            skArc(sketch, "E7.29.2", {"start": v(-19.9, -15.9) * mm, "mid": v(-19.75, -15.99) * mm, "end": v(-19.57, -15.96) * mm});
            skArc(sketch, "E7.29.3", {"start": v(-20.1, -15.63) * mm, "mid": v(-20, -15.76) * mm, "end": v(-19.9, -15.9) * mm});
            skArc(sketch, "E7.29.4", {"start": v(-20.09, -15.3) * mm, "mid": v(-20.15, -15.47) * mm, "end": v(-20.1, -15.63) * mm});
            skArc(sketch, "E7.29.5", {"start": v(-20.09, -15.3) * mm, "mid": v(-20.02, -15.22) * mm, "end": v(-19.96, -15.12) * mm});
            skArc(sketch, "E7.29.6", {"start": v(-19.96, -15.12) * mm, "mid": v(-19.89, -14.82) * mm, "end": v(-20, -14.53) * mm});
            skArc(sketch, "E7.30.0", {"start": v(-17.48, -17.48) * mm, "mid": v(-17.75, -17.33) * mm, "end": v(-18.05, -17.35) * mm});
            skArc(sketch, "E7.30.1", {"start": v(-18.05, -17.35) * mm, "mid": v(-18.16, -17.4) * mm, "end": v(-18.26, -17.45) * mm});
            skArc(sketch, "E7.30.2", {"start": v(-18.58, -17.4) * mm, "mid": v(-18.43, -17.49) * mm, "end": v(-18.26, -17.45) * mm});
            skArc(sketch, "E7.30.3", {"start": v(-18.81, -17.16) * mm, "mid": v(-18.7, -17.28) * mm, "end": v(-18.58, -17.4) * mm});
            skArc(sketch, "E7.30.4", {"start": v(-18.83, -16.84) * mm, "mid": v(-18.88, -17) * mm, "end": v(-18.81, -17.16) * mm});
            skArc(sketch, "E7.30.5", {"start": v(-18.83, -16.84) * mm, "mid": v(-18.76, -16.74) * mm, "end": v(-18.7, -16.64) * mm});
            skArc(sketch, "E7.30.6", {"start": v(-18.7, -16.64) * mm, "mid": v(-18.67, -16.33) * mm, "end": v(-18.8, -16.05) * mm});
            skArc(sketch, "E7.31.0", {"start": v(-16.05, -18.8) * mm, "mid": v(-16.33, -18.67) * mm, "end": v(-16.64, -18.7) * mm});
            skArc(sketch, "E7.31.1", {"start": v(-16.64, -18.7) * mm, "mid": v(-16.74, -18.76) * mm, "end": v(-16.84, -18.83) * mm});
            skArc(sketch, "E7.31.2", {"start": v(-17.16, -18.81) * mm, "mid": v(-17, -18.88) * mm, "end": v(-16.84, -18.83) * mm});
            skArc(sketch, "E7.31.3", {"start": v(-17.4, -18.58) * mm, "mid": v(-17.28, -18.7) * mm, "end": v(-17.16, -18.81) * mm});
            skArc(sketch, "E7.31.4", {"start": v(-17.45, -18.26) * mm, "mid": v(-17.49, -18.43) * mm, "end": v(-17.4, -18.58) * mm});
            skArc(sketch, "E7.31.5", {"start": v(-17.45, -18.26) * mm, "mid": v(-17.4, -18.16) * mm, "end": v(-17.35, -18.05) * mm});
            skArc(sketch, "E7.31.6", {"start": v(-17.35, -18.05) * mm, "mid": v(-17.33, -17.75) * mm, "end": v(-17.48, -17.48) * mm});
            skArc(sketch, "E7.32.0", {"start": v(-14.53, -20) * mm, "mid": v(-14.82, -19.89) * mm, "end": v(-15.12, -19.96) * mm});
            skArc(sketch, "E7.32.1", {"start": v(-15.12, -19.96) * mm, "mid": v(-15.22, -20.02) * mm, "end": v(-15.3, -20.09) * mm});
            skArc(sketch, "E7.32.2", {"start": v(-15.63, -20.1) * mm, "mid": v(-15.47, -20.15) * mm, "end": v(-15.3, -20.09) * mm});
            skArc(sketch, "E7.32.3", {"start": v(-15.9, -19.9) * mm, "mid": v(-15.76, -20) * mm, "end": v(-15.63, -20.1) * mm});
            skArc(sketch, "E7.32.4", {"start": v(-15.96, -19.57) * mm, "mid": v(-15.99, -19.75) * mm, "end": v(-15.9, -19.9) * mm});
            skArc(sketch, "E7.32.5", {"start": v(-15.96, -19.57) * mm, "mid": v(-15.91, -19.47) * mm, "end": v(-15.88, -19.36) * mm});
            skArc(sketch, "E7.32.6", {"start": v(-15.88, -19.36) * mm, "mid": v(-15.88, -19.05) * mm, "end": v(-16.05, -18.8) * mm});
            skArc(sketch, "E7.33.0", {"start": v(-12.91, -21.07) * mm, "mid": v(-13.21, -21) * mm, "end": v(-13.5, -21.08) * mm});
            skArc(sketch, "E7.33.1", {"start": v(-13.5, -21.08) * mm, "mid": v(-13.6, -21.15) * mm, "end": v(-13.68, -21.23) * mm});
            skArc(sketch, "E7.33.2", {"start": v(-14, -21.26) * mm, "mid": v(-13.84, -21.3) * mm, "end": v(-13.68, -21.23) * mm});
            skArc(sketch, "E7.33.3", {"start": v(-14.29, -21.08) * mm, "mid": v(-14.15, -21.17) * mm, "end": v(-14, -21.26) * mm});
            skArc(sketch, "E7.33.4", {"start": v(-14.38, -20.77) * mm, "mid": v(-14.39, -20.94) * mm, "end": v(-14.29, -21.08) * mm});
            skArc(sketch, "E7.33.5", {"start": v(-14.38, -20.77) * mm, "mid": v(-14.34, -20.66) * mm, "end": v(-14.3, -20.54) * mm});
            skArc(sketch, "E7.33.6", {"start": v(-14.3, -20.54) * mm, "mid": v(-14.34, -20.24) * mm, "end": v(-14.53, -20) * mm});
            skArc(sketch, "E7.34.0", {"start": v(-11.22, -22.02) * mm, "mid": v(-11.52, -21.96) * mm, "end": v(-11.81, -22.08) * mm});
            skArc(sketch, "E7.34.1", {"start": v(-11.81, -22.08) * mm, "mid": v(-11.9, -22.15) * mm, "end": v(-11.98, -22.24) * mm});
            skArc(sketch, "E7.34.2", {"start": v(-12.3, -22.3) * mm, "mid": v(-12.12, -22.33) * mm, "end": v(-11.98, -22.24) * mm});
            skArc(sketch, "E7.34.3", {"start": v(-12.59, -22.13) * mm, "mid": v(-12.44, -22.22) * mm, "end": v(-12.3, -22.3) * mm});
            skArc(sketch, "E7.34.4", {"start": v(-12.7, -21.83) * mm, "mid": v(-12.7, -22) * mm, "end": v(-12.59, -22.13) * mm});
            skArc(sketch, "E7.34.5", {"start": v(-12.7, -21.83) * mm, "mid": v(-12.67, -21.72) * mm, "end": v(-12.65, -21.6) * mm});
            skArc(sketch, "E7.34.6", {"start": v(-12.65, -21.6) * mm, "mid": v(-12.7, -21.3) * mm, "end": v(-12.91, -21.07) * mm});
            skArc(sketch, "E7.35.0", {"start": v(-9.46, -22.83) * mm, "mid": v(-9.76, -22.8) * mm, "end": v(-10.04, -22.93) * mm});
            skArc(sketch, "E7.35.1", {"start": v(-10.04, -22.93) * mm, "mid": v(-10.12, -23.02) * mm, "end": v(-10.2, -23.1) * mm});
            skArc(sketch, "E7.35.2", {"start": v(-10.5, -23.2) * mm, "mid": v(-10.34, -23.2) * mm, "end": v(-10.2, -23.1) * mm});
            skArc(sketch, "E7.35.3", {"start": v(-10.81, -23.05) * mm, "mid": v(-10.66, -23.12) * mm, "end": v(-10.5, -23.2) * mm});
            skArc(sketch, "E7.35.4", {"start": v(-10.95, -22.76) * mm, "mid": v(-10.93, -22.93) * mm, "end": v(-10.81, -23.05) * mm});
            skArc(sketch, "E7.35.5", {"start": v(-10.95, -22.76) * mm, "mid": v(-10.93, -22.65) * mm, "end": v(-10.92, -22.53) * mm});
            skArc(sketch, "E7.35.6", {"start": v(-10.92, -22.53) * mm, "mid": v(-11, -22.23) * mm, "end": v(-11.22, -22.02) * mm});
            skArc(sketch, "E7.36.0", {"start": v(-7.64, -23.5) * mm, "mid": v(-7.95, -23.5) * mm, "end": v(-8.21, -23.65) * mm});
            skArc(sketch, "E7.36.1", {"start": v(-8.21, -23.65) * mm, "mid": v(-8.29, -23.74) * mm, "end": v(-8.35, -23.84) * mm});
            skArc(sketch, "E7.36.2", {"start": v(-8.66, -23.95) * mm, "mid": v(-8.48, -23.95) * mm, "end": v(-8.35, -23.84) * mm});
            skArc(sketch, "E7.36.3", {"start": v(-8.97, -23.83) * mm, "mid": v(-8.81, -23.89) * mm, "end": v(-8.66, -23.95) * mm});
            skArc(sketch, "E7.36.4", {"start": v(-9.13, -23.55) * mm, "mid": v(-9.1, -23.72) * mm, "end": v(-8.97, -23.83) * mm});
            skArc(sketch, "E7.36.5", {"start": v(-9.13, -23.55) * mm, "mid": v(-9.12, -23.43) * mm, "end": v(-9.12, -23.32) * mm});
            skArc(sketch, "E7.36.6", {"start": v(-9.12, -23.32) * mm, "mid": v(-9.22, -23.03) * mm, "end": v(-9.46, -22.83) * mm});
            skArc(sketch, "E7.37.0", {"start": v(-5.77, -24.03) * mm, "mid": v(-6.08, -24.05) * mm, "end": v(-6.33, -24.22) * mm});
            skArc(sketch, "E7.37.1", {"start": v(-6.33, -24.22) * mm, "mid": v(-6.4, -24.32) * mm, "end": v(-6.45, -24.42) * mm});
            skArc(sketch, "E7.37.2", {"start": v(-6.75, -24.55) * mm, "mid": v(-6.58, -24.54) * mm, "end": v(-6.45, -24.42) * mm});
            skArc(sketch, "E7.37.3", {"start": v(-7.07, -24.46) * mm, "mid": v(-6.91, -24.5) * mm, "end": v(-6.75, -24.55) * mm});
            skArc(sketch, "E7.37.4", {"start": v(-7.26, -24.2) * mm, "mid": v(-7.21, -24.36) * mm, "end": v(-7.07, -24.46) * mm});
            skArc(sketch, "E7.37.5", {"start": v(-7.26, -24.2) * mm, "mid": v(-7.25, -24.08) * mm, "end": v(-7.26, -23.96) * mm});
            skArc(sketch, "E7.37.6", {"start": v(-7.26, -23.96) * mm, "mid": v(-7.38, -23.68) * mm, "end": v(-7.64, -23.5) * mm});
            skArc(sketch, "E7.38.0", {"start": v(-3.87, -24.4) * mm, "mid": v(-4.17, -24.45) * mm, "end": v(-4.41, -24.64) * mm});
            skArc(sketch, "E7.38.1", {"start": v(-4.41, -24.64) * mm, "mid": v(-4.47, -24.74) * mm, "end": v(-4.52, -24.85) * mm});
            skArc(sketch, "E7.38.2", {"start": v(-4.8, -25) * mm, "mid": v(-4.63, -24.98) * mm, "end": v(-4.52, -24.85) * mm});
            skArc(sketch, "E7.38.3", {"start": v(-5.13, -24.94) * mm, "mid": v(-4.97, -24.97) * mm, "end": v(-4.8, -25) * mm});
            skArc(sketch, "E7.38.4", {"start": v(-5.33, -24.69) * mm, "mid": v(-5.28, -24.85) * mm, "end": v(-5.13, -24.94) * mm});
            skArc(sketch, "E7.38.5", {"start": v(-5.33, -24.69) * mm, "mid": v(-5.34, -24.57) * mm, "end": v(-5.36, -24.46) * mm});
            skArc(sketch, "E7.38.6", {"start": v(-5.36, -24.46) * mm, "mid": v(-5.5, -24.18) * mm, "end": v(-5.77, -24.03) * mm});
            skArc(sketch, "E7.39.0", {"start": v(-1.94, -24.64) * mm, "mid": v(-2.24, -24.7) * mm, "end": v(-2.46, -24.91) * mm});
            skArc(sketch, "E7.39.1", {"start": v(-2.46, -24.91) * mm, "mid": v(-2.52, -25.02) * mm, "end": v(-2.55, -25.13) * mm});
            skArc(sketch, "E7.39.2", {"start": v(-2.83, -25.3) * mm, "mid": v(-2.66, -25.27) * mm, "end": v(-2.55, -25.13) * mm});
            skArc(sketch, "E7.39.3", {"start": v(-3.16, -25.27) * mm, "mid": v(-3, -25.29) * mm, "end": v(-2.83, -25.3) * mm});
            skArc(sketch, "E7.39.4", {"start": v(-3.38, -25.03) * mm, "mid": v(-3.31, -25.19) * mm, "end": v(-3.16, -25.27) * mm});
            skArc(sketch, "E7.39.5", {"start": v(-3.38, -25.03) * mm, "mid": v(-3.4, -24.91) * mm, "end": v(-3.42, -24.8) * mm});
            skArc(sketch, "E7.39.6", {"start": v(-3.42, -24.8) * mm, "mid": v(-3.59, -24.54) * mm, "end": v(-3.87, -24.4) * mm});
            skArc(sketch, "E7.40.0", {"start": v(0, -24.71) * mm, "mid": v(-0.3, -24.8) * mm, "end": v(-0.5, -25.03) * mm});
            skArc(sketch, "E7.40.1", {"start": v(-0.5, -25.03) * mm, "mid": v(-0.54, -25.14) * mm, "end": v(-0.58, -25.25) * mm});
            skArc(sketch, "E7.40.2", {"start": v(-0.83, -25.45) * mm, "mid": v(-0.67, -25.4) * mm, "end": v(-0.58, -25.25) * mm});
            skArc(sketch, "E7.40.3", {"start": v(-1.17, -25.44) * mm, "mid": v(-1, -25.44) * mm, "end": v(-0.83, -25.45) * mm});
            skArc(sketch, "E7.40.4", {"start": v(-1.4, -25.22) * mm, "mid": v(-1.33, -25.37) * mm, "end": v(-1.17, -25.44) * mm});
            skArc(sketch, "E7.40.5", {"start": v(-1.4, -25.22) * mm, "mid": v(-1.43, -25.1) * mm, "end": v(-1.46, -25) * mm});
            skArc(sketch, "E7.40.6", {"start": v(-1.46, -25) * mm, "mid": v(-1.65, -24.75) * mm, "end": v(-1.94, -24.64) * mm});
            skArc(sketch, "E7.41.0", {"start": v(1.94, -24.64) * mm, "mid": v(1.65, -24.75) * mm, "end": v(1.46, -25) * mm});
            skArc(sketch, "E7.41.1", {"start": v(1.46, -25) * mm, "mid": v(1.43, -25.1) * mm, "end": v(1.4, -25.22) * mm});
            skArc(sketch, "E7.41.2", {"start": v(1.17, -25.44) * mm, "mid": v(1.33, -25.37) * mm, "end": v(1.4, -25.22) * mm});
            skArc(sketch, "E7.41.3", {"start": v(0.83, -25.45) * mm, "mid": v(1, -25.44) * mm, "end": v(1.17, -25.44) * mm});
            skArc(sketch, "E7.41.4", {"start": v(0.58, -25.25) * mm, "mid": v(0.67, -25.4) * mm, "end": v(0.83, -25.45) * mm});
            skArc(sketch, "E7.41.5", {"start": v(0.58, -25.25) * mm, "mid": v(0.54, -25.14) * mm, "end": v(0.5, -25.03) * mm});
            skArc(sketch, "E7.41.6", {"start": v(0.5, -25.03) * mm, "mid": v(0.3, -24.8) * mm, "end": v(0, -24.71) * mm});
            skArc(sketch, "E7.42.0", {"start": v(3.87, -24.4) * mm, "mid": v(3.59, -24.54) * mm, "end": v(3.42, -24.8) * mm});
            skArc(sketch, "E7.42.1", {"start": v(3.42, -24.8) * mm, "mid": v(3.4, -24.91) * mm, "end": v(3.38, -25.03) * mm});
            skArc(sketch, "E7.42.2", {"start": v(3.16, -25.27) * mm, "mid": v(3.31, -25.19) * mm, "end": v(3.38, -25.03) * mm});
            skArc(sketch, "E7.42.3", {"start": v(2.83, -25.3) * mm, "mid": v(3, -25.29) * mm, "end": v(3.16, -25.27) * mm});
            skArc(sketch, "E7.42.4", {"start": v(2.55, -25.13) * mm, "mid": v(2.66, -25.27) * mm, "end": v(2.83, -25.3) * mm});
            skArc(sketch, "E7.42.5", {"start": v(2.55, -25.13) * mm, "mid": v(2.52, -25.02) * mm, "end": v(2.46, -24.91) * mm});
            skArc(sketch, "E7.42.6", {"start": v(2.46, -24.91) * mm, "mid": v(2.24, -24.7) * mm, "end": v(1.94, -24.64) * mm});
            skArc(sketch, "E7.43.0", {"start": v(5.77, -24.03) * mm, "mid": v(5.5, -24.18) * mm, "end": v(5.36, -24.46) * mm});
            skArc(sketch, "E7.43.1", {"start": v(5.36, -24.46) * mm, "mid": v(5.34, -24.57) * mm, "end": v(5.33, -24.69) * mm});
            skArc(sketch, "E7.43.2", {"start": v(5.13, -24.94) * mm, "mid": v(5.28, -24.85) * mm, "end": v(5.33, -24.69) * mm});
            skArc(sketch, "E7.43.3", {"start": v(4.8, -25) * mm, "mid": v(4.97, -24.97) * mm, "end": v(5.13, -24.94) * mm});
            skArc(sketch, "E7.43.4", {"start": v(4.52, -24.85) * mm, "mid": v(4.63, -24.98) * mm, "end": v(4.8, -25) * mm});
            skArc(sketch, "E7.43.5", {"start": v(4.52, -24.85) * mm, "mid": v(4.47, -24.74) * mm, "end": v(4.41, -24.64) * mm});
            skArc(sketch, "E7.43.6", {"start": v(4.41, -24.64) * mm, "mid": v(4.17, -24.45) * mm, "end": v(3.87, -24.4) * mm});
            skArc(sketch, "E7.44.0", {"start": v(7.64, -23.5) * mm, "mid": v(7.38, -23.68) * mm, "end": v(7.26, -23.96) * mm});
            skArc(sketch, "E7.44.1", {"start": v(7.26, -23.96) * mm, "mid": v(7.25, -24.08) * mm, "end": v(7.26, -24.2) * mm});
            skArc(sketch, "E7.44.2", {"start": v(7.07, -24.46) * mm, "mid": v(7.21, -24.36) * mm, "end": v(7.26, -24.2) * mm});
            skArc(sketch, "E7.44.3", {"start": v(6.75, -24.55) * mm, "mid": v(6.91, -24.5) * mm, "end": v(7.07, -24.46) * mm});
            skArc(sketch, "E7.44.4", {"start": v(6.45, -24.42) * mm, "mid": v(6.58, -24.54) * mm, "end": v(6.75, -24.55) * mm});
            skArc(sketch, "E7.44.5", {"start": v(6.45, -24.42) * mm, "mid": v(6.4, -24.32) * mm, "end": v(6.33, -24.22) * mm});
            skArc(sketch, "E7.44.6", {"start": v(6.33, -24.22) * mm, "mid": v(6.08, -24.05) * mm, "end": v(5.77, -24.03) * mm});
            skArc(sketch, "E7.45.0", {"start": v(9.46, -22.83) * mm, "mid": v(9.22, -23.03) * mm, "end": v(9.12, -23.32) * mm});
            skArc(sketch, "E7.45.1", {"start": v(9.12, -23.32) * mm, "mid": v(9.12, -23.43) * mm, "end": v(9.13, -23.55) * mm});
            skArc(sketch, "E7.45.2", {"start": v(8.97, -23.83) * mm, "mid": v(9.1, -23.72) * mm, "end": v(9.13, -23.55) * mm});
            skArc(sketch, "E7.45.3", {"start": v(8.66, -23.95) * mm, "mid": v(8.81, -23.89) * mm, "end": v(8.97, -23.83) * mm});
            skArc(sketch, "E7.45.4", {"start": v(8.35, -23.84) * mm, "mid": v(8.48, -23.95) * mm, "end": v(8.66, -23.95) * mm});
            skArc(sketch, "E7.45.5", {"start": v(8.35, -23.84) * mm, "mid": v(8.29, -23.74) * mm, "end": v(8.21, -23.65) * mm});
            skArc(sketch, "E7.45.6", {"start": v(8.21, -23.65) * mm, "mid": v(7.95, -23.5) * mm, "end": v(7.64, -23.5) * mm});
            skArc(sketch, "E7.46.0", {"start": v(11.22, -22.02) * mm, "mid": v(11, -22.23) * mm, "end": v(10.92, -22.53) * mm});
            skArc(sketch, "E7.46.1", {"start": v(10.92, -22.53) * mm, "mid": v(10.93, -22.65) * mm, "end": v(10.95, -22.76) * mm});
            skArc(sketch, "E7.46.2", {"start": v(10.81, -23.05) * mm, "mid": v(10.93, -22.93) * mm, "end": v(10.95, -22.76) * mm});
            skArc(sketch, "E7.46.3", {"start": v(10.5, -23.2) * mm, "mid": v(10.66, -23.12) * mm, "end": v(10.81, -23.05) * mm});
            skArc(sketch, "E7.46.4", {"start": v(10.2, -23.1) * mm, "mid": v(10.34, -23.2) * mm, "end": v(10.5, -23.2) * mm});
            skArc(sketch, "E7.46.5", {"start": v(10.2, -23.1) * mm, "mid": v(10.12, -23.02) * mm, "end": v(10.04, -22.93) * mm});
            skArc(sketch, "E7.46.6", {"start": v(10.04, -22.93) * mm, "mid": v(9.76, -22.8) * mm, "end": v(9.46, -22.83) * mm});
            skArc(sketch, "E7.47.0", {"start": v(12.91, -21.07) * mm, "mid": v(12.7, -21.3) * mm, "end": v(12.65, -21.6) * mm});
            skArc(sketch, "E7.47.1", {"start": v(12.65, -21.6) * mm, "mid": v(12.67, -21.72) * mm, "end": v(12.7, -21.83) * mm});
            skArc(sketch, "E7.47.2", {"start": v(12.59, -22.13) * mm, "mid": v(12.7, -22) * mm, "end": v(12.7, -21.83) * mm});
            skArc(sketch, "E7.47.3", {"start": v(12.3, -22.3) * mm, "mid": v(12.44, -22.22) * mm, "end": v(12.59, -22.13) * mm});
            skArc(sketch, "E7.47.4", {"start": v(11.98, -22.24) * mm, "mid": v(12.12, -22.33) * mm, "end": v(12.3, -22.3) * mm});
            skArc(sketch, "E7.47.5", {"start": v(11.98, -22.24) * mm, "mid": v(11.9, -22.15) * mm, "end": v(11.81, -22.08) * mm});
            skArc(sketch, "E7.47.6", {"start": v(11.81, -22.08) * mm, "mid": v(11.52, -21.96) * mm, "end": v(11.22, -22.02) * mm});
            skArc(sketch, "E7.48.0", {"start": v(14.53, -20) * mm, "mid": v(14.34, -20.24) * mm, "end": v(14.3, -20.54) * mm});
            skArc(sketch, "E7.48.1", {"start": v(14.3, -20.54) * mm, "mid": v(14.34, -20.66) * mm, "end": v(14.38, -20.77) * mm});
            skArc(sketch, "E7.48.2", {"start": v(14.29, -21.08) * mm, "mid": v(14.39, -20.94) * mm, "end": v(14.38, -20.77) * mm});
            skArc(sketch, "E7.48.3", {"start": v(14, -21.26) * mm, "mid": v(14.15, -21.17) * mm, "end": v(14.29, -21.08) * mm});
            skArc(sketch, "E7.48.4", {"start": v(13.68, -21.23) * mm, "mid": v(13.84, -21.3) * mm, "end": v(14, -21.26) * mm});
            skArc(sketch, "E7.48.5", {"start": v(13.68, -21.23) * mm, "mid": v(13.6, -21.15) * mm, "end": v(13.5, -21.08) * mm});
            skArc(sketch, "E7.48.6", {"start": v(13.5, -21.08) * mm, "mid": v(13.21, -21) * mm, "end": v(12.91, -21.07) * mm});
            skArc(sketch, "E7.49.0", {"start": v(16.05, -18.8) * mm, "mid": v(15.88, -19.05) * mm, "end": v(15.88, -19.36) * mm});
            skArc(sketch, "E7.49.1", {"start": v(15.88, -19.36) * mm, "mid": v(15.91, -19.47) * mm, "end": v(15.96, -19.57) * mm});
            skArc(sketch, "E7.49.2", {"start": v(15.9, -19.9) * mm, "mid": v(15.99, -19.75) * mm, "end": v(15.96, -19.57) * mm});
            skArc(sketch, "E7.49.3", {"start": v(15.63, -20.1) * mm, "mid": v(15.76, -20) * mm, "end": v(15.9, -19.9) * mm});
            skArc(sketch, "E7.49.4", {"start": v(15.3, -20.09) * mm, "mid": v(15.47, -20.15) * mm, "end": v(15.63, -20.1) * mm});
            skArc(sketch, "E7.49.5", {"start": v(15.3, -20.09) * mm, "mid": v(15.22, -20.02) * mm, "end": v(15.12, -19.96) * mm});
            skArc(sketch, "E7.49.6", {"start": v(15.12, -19.96) * mm, "mid": v(14.82, -19.89) * mm, "end": v(14.53, -20) * mm});
            skArc(sketch, "E7.50.0", {"start": v(17.48, -17.48) * mm, "mid": v(17.33, -17.75) * mm, "end": v(17.35, -18.05) * mm});
            skArc(sketch, "E7.50.1", {"start": v(17.35, -18.05) * mm, "mid": v(17.4, -18.16) * mm, "end": v(17.45, -18.26) * mm});
            skArc(sketch, "E7.50.2", {"start": v(17.4, -18.58) * mm, "mid": v(17.49, -18.43) * mm, "end": v(17.45, -18.26) * mm});
            skArc(sketch, "E7.50.3", {"start": v(17.16, -18.81) * mm, "mid": v(17.28, -18.7) * mm, "end": v(17.4, -18.58) * mm});
            skArc(sketch, "E7.50.4", {"start": v(16.84, -18.83) * mm, "mid": v(17, -18.88) * mm, "end": v(17.16, -18.81) * mm});
            skArc(sketch, "E7.50.5", {"start": v(16.84, -18.83) * mm, "mid": v(16.74, -18.76) * mm, "end": v(16.64, -18.7) * mm});
            skArc(sketch, "E7.50.6", {"start": v(16.64, -18.7) * mm, "mid": v(16.33, -18.67) * mm, "end": v(16.05, -18.8) * mm});
            skArc(sketch, "E7.51.0", {"start": v(18.8, -16.05) * mm, "mid": v(18.67, -16.33) * mm, "end": v(18.7, -16.64) * mm});
            skArc(sketch, "E7.51.1", {"start": v(18.7, -16.64) * mm, "mid": v(18.76, -16.74) * mm, "end": v(18.83, -16.84) * mm});
            skArc(sketch, "E7.51.2", {"start": v(18.81, -17.16) * mm, "mid": v(18.88, -17) * mm, "end": v(18.83, -16.84) * mm});
            skArc(sketch, "E7.51.3", {"start": v(18.58, -17.4) * mm, "mid": v(18.7, -17.28) * mm, "end": v(18.81, -17.16) * mm});
            skArc(sketch, "E7.51.4", {"start": v(18.26, -17.45) * mm, "mid": v(18.43, -17.49) * mm, "end": v(18.58, -17.4) * mm});
            skArc(sketch, "E7.51.5", {"start": v(18.26, -17.45) * mm, "mid": v(18.16, -17.4) * mm, "end": v(18.05, -17.35) * mm});
            skArc(sketch, "E7.51.6", {"start": v(18.05, -17.35) * mm, "mid": v(17.75, -17.33) * mm, "end": v(17.48, -17.48) * mm});
            skArc(sketch, "E7.52.0", {"start": v(20, -14.53) * mm, "mid": v(19.89, -14.82) * mm, "end": v(19.96, -15.12) * mm});
            skArc(sketch, "E7.52.1", {"start": v(19.96, -15.12) * mm, "mid": v(20.02, -15.22) * mm, "end": v(20.09, -15.3) * mm});
            skArc(sketch, "E7.52.2", {"start": v(20.1, -15.63) * mm, "mid": v(20.15, -15.47) * mm, "end": v(20.09, -15.3) * mm});
            skArc(sketch, "E7.52.3", {"start": v(19.9, -15.9) * mm, "mid": v(20, -15.76) * mm, "end": v(20.1, -15.63) * mm});
            skArc(sketch, "E7.52.4", {"start": v(19.57, -15.96) * mm, "mid": v(19.75, -15.99) * mm, "end": v(19.9, -15.9) * mm});
            skArc(sketch, "E7.52.5", {"start": v(19.57, -15.96) * mm, "mid": v(19.47, -15.91) * mm, "end": v(19.36, -15.88) * mm});
            skArc(sketch, "E7.52.6", {"start": v(19.36, -15.88) * mm, "mid": v(19.05, -15.88) * mm, "end": v(18.8, -16.05) * mm});
            skArc(sketch, "E7.53.0", {"start": v(21.07, -12.91) * mm, "mid": v(21, -13.21) * mm, "end": v(21.08, -13.5) * mm});
            skArc(sketch, "E7.53.1", {"start": v(21.08, -13.5) * mm, "mid": v(21.15, -13.6) * mm, "end": v(21.23, -13.68) * mm});
            skArc(sketch, "E7.53.2", {"start": v(21.26, -14) * mm, "mid": v(21.3, -13.84) * mm, "end": v(21.23, -13.68) * mm});
            skArc(sketch, "E7.53.3", {"start": v(21.08, -14.29) * mm, "mid": v(21.17, -14.15) * mm, "end": v(21.26, -14) * mm});
            skArc(sketch, "E7.53.4", {"start": v(20.77, -14.38) * mm, "mid": v(20.94, -14.39) * mm, "end": v(21.08, -14.29) * mm});
            skArc(sketch, "E7.53.5", {"start": v(20.77, -14.38) * mm, "mid": v(20.66, -14.34) * mm, "end": v(20.54, -14.3) * mm});
            skArc(sketch, "E7.53.6", {"start": v(20.54, -14.3) * mm, "mid": v(20.24, -14.34) * mm, "end": v(20, -14.53) * mm});
            skArc(sketch, "E7.54.0", {"start": v(22.02, -11.22) * mm, "mid": v(21.96, -11.52) * mm, "end": v(22.08, -11.81) * mm});
            skArc(sketch, "E7.54.1", {"start": v(22.08, -11.81) * mm, "mid": v(22.15, -11.9) * mm, "end": v(22.24, -11.98) * mm});
            skArc(sketch, "E7.54.2", {"start": v(22.3, -12.3) * mm, "mid": v(22.33, -12.12) * mm, "end": v(22.24, -11.98) * mm});
            skArc(sketch, "E7.54.3", {"start": v(22.13, -12.59) * mm, "mid": v(22.22, -12.44) * mm, "end": v(22.3, -12.3) * mm});
            skArc(sketch, "E7.54.4", {"start": v(21.83, -12.7) * mm, "mid": v(22, -12.7) * mm, "end": v(22.13, -12.59) * mm});
            skArc(sketch, "E7.54.5", {"start": v(21.83, -12.7) * mm, "mid": v(21.72, -12.67) * mm, "end": v(21.6, -12.65) * mm});
            skArc(sketch, "E7.54.6", {"start": v(21.6, -12.65) * mm, "mid": v(21.3, -12.7) * mm, "end": v(21.07, -12.91) * mm});
            skArc(sketch, "E7.55.0", {"start": v(22.83, -9.46) * mm, "mid": v(22.8, -9.76) * mm, "end": v(22.93, -10.04) * mm});
            skArc(sketch, "E7.55.1", {"start": v(22.93, -10.04) * mm, "mid": v(23.02, -10.12) * mm, "end": v(23.1, -10.2) * mm});
            skArc(sketch, "E7.55.2", {"start": v(23.2, -10.5) * mm, "mid": v(23.2, -10.34) * mm, "end": v(23.1, -10.2) * mm});
            skArc(sketch, "E7.55.3", {"start": v(23.05, -10.81) * mm, "mid": v(23.12, -10.66) * mm, "end": v(23.2, -10.5) * mm});
            skArc(sketch, "E7.55.4", {"start": v(22.76, -10.95) * mm, "mid": v(22.93, -10.93) * mm, "end": v(23.05, -10.81) * mm});
            skArc(sketch, "E7.55.5", {"start": v(22.76, -10.95) * mm, "mid": v(22.65, -10.93) * mm, "end": v(22.53, -10.92) * mm});
            skArc(sketch, "E7.55.6", {"start": v(22.53, -10.92) * mm, "mid": v(22.23, -11) * mm, "end": v(22.02, -11.22) * mm});
            skArc(sketch, "E7.56.0", {"start": v(23.5, -7.64) * mm, "mid": v(23.5, -7.95) * mm, "end": v(23.65, -8.21) * mm});
            skArc(sketch, "E7.56.1", {"start": v(23.65, -8.21) * mm, "mid": v(23.74, -8.29) * mm, "end": v(23.84, -8.35) * mm});
            skArc(sketch, "E7.56.2", {"start": v(23.95, -8.66) * mm, "mid": v(23.95, -8.48) * mm, "end": v(23.84, -8.35) * mm});
            skArc(sketch, "E7.56.3", {"start": v(23.83, -8.97) * mm, "mid": v(23.89, -8.81) * mm, "end": v(23.95, -8.66) * mm});
            skArc(sketch, "E7.56.4", {"start": v(23.55, -9.13) * mm, "mid": v(23.72, -9.1) * mm, "end": v(23.83, -8.97) * mm});
            skArc(sketch, "E7.56.5", {"start": v(23.55, -9.13) * mm, "mid": v(23.43, -9.12) * mm, "end": v(23.32, -9.12) * mm});
            skArc(sketch, "E7.56.6", {"start": v(23.32, -9.12) * mm, "mid": v(23.03, -9.22) * mm, "end": v(22.83, -9.46) * mm});
            skArc(sketch, "E7.57.0", {"start": v(24.03, -5.77) * mm, "mid": v(24.05, -6.08) * mm, "end": v(24.22, -6.33) * mm});
            skArc(sketch, "E7.57.1", {"start": v(24.22, -6.33) * mm, "mid": v(24.32, -6.4) * mm, "end": v(24.42, -6.45) * mm});
            skArc(sketch, "E7.57.2", {"start": v(24.55, -6.75) * mm, "mid": v(24.54, -6.58) * mm, "end": v(24.42, -6.45) * mm});
            skArc(sketch, "E7.57.3", {"start": v(24.46, -7.07) * mm, "mid": v(24.5, -6.91) * mm, "end": v(24.55, -6.75) * mm});
            skArc(sketch, "E7.57.4", {"start": v(24.2, -7.26) * mm, "mid": v(24.36, -7.21) * mm, "end": v(24.46, -7.07) * mm});
            skArc(sketch, "E7.57.5", {"start": v(24.2, -7.26) * mm, "mid": v(24.08, -7.25) * mm, "end": v(23.96, -7.26) * mm});
            skArc(sketch, "E7.57.6", {"start": v(23.96, -7.26) * mm, "mid": v(23.68, -7.38) * mm, "end": v(23.5, -7.64) * mm});
            skArc(sketch, "E7.58.0", {"start": v(24.4, -3.87) * mm, "mid": v(24.45, -4.17) * mm, "end": v(24.64, -4.41) * mm});
            skArc(sketch, "E7.58.1", {"start": v(24.64, -4.41) * mm, "mid": v(24.74, -4.47) * mm, "end": v(24.85, -4.52) * mm});
            skArc(sketch, "E7.58.2", {"start": v(25, -4.8) * mm, "mid": v(24.98, -4.63) * mm, "end": v(24.85, -4.52) * mm});
            skArc(sketch, "E7.58.3", {"start": v(24.94, -5.13) * mm, "mid": v(24.97, -4.97) * mm, "end": v(25, -4.8) * mm});
            skArc(sketch, "E7.58.4", {"start": v(24.69, -5.33) * mm, "mid": v(24.85, -5.28) * mm, "end": v(24.94, -5.13) * mm});
            skArc(sketch, "E7.58.5", {"start": v(24.69, -5.33) * mm, "mid": v(24.57, -5.34) * mm, "end": v(24.46, -5.36) * mm});
            skArc(sketch, "E7.58.6", {"start": v(24.46, -5.36) * mm, "mid": v(24.18, -5.5) * mm, "end": v(24.03, -5.77) * mm});
            skArc(sketch, "E7.59.0", {"start": v(24.64, -1.94) * mm, "mid": v(24.7, -2.24) * mm, "end": v(24.91, -2.46) * mm});
            skArc(sketch, "E7.59.1", {"start": v(24.91, -2.46) * mm, "mid": v(25.02, -2.52) * mm, "end": v(25.13, -2.55) * mm});
            skArc(sketch, "E7.59.2", {"start": v(25.3, -2.83) * mm, "mid": v(25.27, -2.66) * mm, "end": v(25.13, -2.55) * mm});
            skArc(sketch, "E7.59.3", {"start": v(25.27, -3.16) * mm, "mid": v(25.29, -3) * mm, "end": v(25.3, -2.83) * mm});
            skArc(sketch, "E7.59.4", {"start": v(25.03, -3.38) * mm, "mid": v(25.19, -3.31) * mm, "end": v(25.27, -3.16) * mm});
            skArc(sketch, "E7.59.5", {"start": v(25.03, -3.38) * mm, "mid": v(24.91, -3.4) * mm, "end": v(24.8, -3.42) * mm});
            skArc(sketch, "E7.59.6", {"start": v(24.8, -3.42) * mm, "mid": v(24.54, -3.59) * mm, "end": v(24.4, -3.87) * mm});
            skArc(sketch, "E7.60.0", {"start": v(24.71, 0) * mm, "mid": v(24.8, -0.3) * mm, "end": v(25.03, -0.5) * mm});
            skArc(sketch, "E7.60.1", {"start": v(25.03, -0.5) * mm, "mid": v(25.14, -0.54) * mm, "end": v(25.25, -0.58) * mm});
            skArc(sketch, "E7.60.2", {"start": v(25.45, -0.83) * mm, "mid": v(25.4, -0.67) * mm, "end": v(25.25, -0.58) * mm});
            skArc(sketch, "E7.60.3", {"start": v(25.44, -1.17) * mm, "mid": v(25.44, -1) * mm, "end": v(25.45, -0.83) * mm});
            skArc(sketch, "E7.60.4", {"start": v(25.22, -1.4) * mm, "mid": v(25.37, -1.33) * mm, "end": v(25.44, -1.17) * mm});
            skArc(sketch, "E7.60.5", {"start": v(25.22, -1.4) * mm, "mid": v(25.1, -1.43) * mm, "end": v(25, -1.46) * mm});
            skArc(sketch, "E7.60.6", {"start": v(25, -1.46) * mm, "mid": v(24.75, -1.65) * mm, "end": v(24.64, -1.94) * mm});
            skArc(sketch, "E7.61.0", {"start": v(24.64, 1.94) * mm, "mid": v(24.75, 1.65) * mm, "end": v(25, 1.46) * mm});
            skArc(sketch, "E7.61.1", {"start": v(25, 1.46) * mm, "mid": v(25.1, 1.43) * mm, "end": v(25.22, 1.4) * mm});
            skArc(sketch, "E7.61.2", {"start": v(25.44, 1.17) * mm, "mid": v(25.37, 1.33) * mm, "end": v(25.22, 1.4) * mm});
            skArc(sketch, "E7.61.3", {"start": v(25.45, 0.83) * mm, "mid": v(25.44, 1) * mm, "end": v(25.44, 1.17) * mm});
            skArc(sketch, "E7.61.4", {"start": v(25.25, 0.58) * mm, "mid": v(25.4, 0.67) * mm, "end": v(25.45, 0.83) * mm});
            skArc(sketch, "E7.61.5", {"start": v(25.25, 0.58) * mm, "mid": v(25.14, 0.54) * mm, "end": v(25.03, 0.5) * mm});
            skArc(sketch, "E7.61.6", {"start": v(25.03, 0.5) * mm, "mid": v(24.8, 0.3) * mm, "end": v(24.71, 0) * mm});
            skArc(sketch, "E7.62.0", {"start": v(24.4, 3.87) * mm, "mid": v(24.54, 3.59) * mm, "end": v(24.8, 3.42) * mm});
            skArc(sketch, "E7.62.1", {"start": v(24.8, 3.42) * mm, "mid": v(24.91, 3.4) * mm, "end": v(25.03, 3.38) * mm});
            skArc(sketch, "E7.62.2", {"start": v(25.27, 3.16) * mm, "mid": v(25.19, 3.31) * mm, "end": v(25.03, 3.38) * mm});
            skArc(sketch, "E7.62.3", {"start": v(25.3, 2.83) * mm, "mid": v(25.29, 3) * mm, "end": v(25.27, 3.16) * mm});
            skArc(sketch, "E7.62.4", {"start": v(25.13, 2.55) * mm, "mid": v(25.27, 2.66) * mm, "end": v(25.3, 2.83) * mm});
            skArc(sketch, "E7.62.5", {"start": v(25.13, 2.55) * mm, "mid": v(25.02, 2.52) * mm, "end": v(24.91, 2.46) * mm});
            skArc(sketch, "E7.62.6", {"start": v(24.91, 2.46) * mm, "mid": v(24.7, 2.24) * mm, "end": v(24.64, 1.94) * mm});
            skArc(sketch, "E7.63.0", {"start": v(24.03, 5.77) * mm, "mid": v(24.18, 5.5) * mm, "end": v(24.46, 5.36) * mm});
            skArc(sketch, "E7.63.1", {"start": v(24.46, 5.36) * mm, "mid": v(24.57, 5.34) * mm, "end": v(24.69, 5.33) * mm});
            skArc(sketch, "E7.63.2", {"start": v(24.94, 5.13) * mm, "mid": v(24.85, 5.28) * mm, "end": v(24.69, 5.33) * mm});
            skArc(sketch, "E7.63.3", {"start": v(25, 4.8) * mm, "mid": v(24.97, 4.97) * mm, "end": v(24.94, 5.13) * mm});
            skArc(sketch, "E7.63.4", {"start": v(24.85, 4.52) * mm, "mid": v(24.98, 4.63) * mm, "end": v(25, 4.8) * mm});
            skArc(sketch, "E7.63.5", {"start": v(24.85, 4.52) * mm, "mid": v(24.74, 4.47) * mm, "end": v(24.64, 4.41) * mm});
            skArc(sketch, "E7.63.6", {"start": v(24.64, 4.41) * mm, "mid": v(24.45, 4.17) * mm, "end": v(24.4, 3.87) * mm});
            skArc(sketch, "E7.64.0", {"start": v(23.5, 7.64) * mm, "mid": v(23.68, 7.38) * mm, "end": v(23.96, 7.26) * mm});
            skArc(sketch, "E7.64.1", {"start": v(23.96, 7.26) * mm, "mid": v(24.08, 7.25) * mm, "end": v(24.2, 7.26) * mm});
            skArc(sketch, "E7.64.2", {"start": v(24.46, 7.07) * mm, "mid": v(24.36, 7.21) * mm, "end": v(24.2, 7.26) * mm});
            skArc(sketch, "E7.64.3", {"start": v(24.55, 6.75) * mm, "mid": v(24.5, 6.91) * mm, "end": v(24.46, 7.07) * mm});
            skArc(sketch, "E7.64.4", {"start": v(24.42, 6.45) * mm, "mid": v(24.54, 6.58) * mm, "end": v(24.55, 6.75) * mm});
            skArc(sketch, "E7.64.5", {"start": v(24.42, 6.45) * mm, "mid": v(24.32, 6.4) * mm, "end": v(24.22, 6.33) * mm});
            skArc(sketch, "E7.64.6", {"start": v(24.22, 6.33) * mm, "mid": v(24.05, 6.08) * mm, "end": v(24.03, 5.77) * mm});
            skArc(sketch, "E7.65.0", {"start": v(22.83, 9.46) * mm, "mid": v(23.03, 9.22) * mm, "end": v(23.32, 9.12) * mm});
            skArc(sketch, "E7.65.1", {"start": v(23.32, 9.12) * mm, "mid": v(23.43, 9.12) * mm, "end": v(23.55, 9.13) * mm});
            skArc(sketch, "E7.65.2", {"start": v(23.83, 8.97) * mm, "mid": v(23.72, 9.1) * mm, "end": v(23.55, 9.13) * mm});
            skArc(sketch, "E7.65.3", {"start": v(23.95, 8.66) * mm, "mid": v(23.89, 8.81) * mm, "end": v(23.83, 8.97) * mm});
            skArc(sketch, "E7.65.4", {"start": v(23.84, 8.35) * mm, "mid": v(23.95, 8.48) * mm, "end": v(23.95, 8.66) * mm});
            skArc(sketch, "E7.65.5", {"start": v(23.84, 8.35) * mm, "mid": v(23.74, 8.29) * mm, "end": v(23.65, 8.21) * mm});
            skArc(sketch, "E7.65.6", {"start": v(23.65, 8.21) * mm, "mid": v(23.5, 7.95) * mm, "end": v(23.5, 7.64) * mm});
            skArc(sketch, "E7.66.0", {"start": v(22.02, 11.22) * mm, "mid": v(22.23, 11) * mm, "end": v(22.53, 10.92) * mm});
            skArc(sketch, "E7.66.1", {"start": v(22.53, 10.92) * mm, "mid": v(22.65, 10.93) * mm, "end": v(22.76, 10.95) * mm});
            skArc(sketch, "E7.66.2", {"start": v(23.05, 10.81) * mm, "mid": v(22.93, 10.93) * mm, "end": v(22.76, 10.95) * mm});
            skArc(sketch, "E7.66.3", {"start": v(23.2, 10.5) * mm, "mid": v(23.12, 10.66) * mm, "end": v(23.05, 10.81) * mm});
            skArc(sketch, "E7.66.4", {"start": v(23.1, 10.2) * mm, "mid": v(23.2, 10.34) * mm, "end": v(23.2, 10.5) * mm});
            skArc(sketch, "E7.66.5", {"start": v(23.1, 10.2) * mm, "mid": v(23.02, 10.12) * mm, "end": v(22.93, 10.04) * mm});
            skArc(sketch, "E7.66.6", {"start": v(22.93, 10.04) * mm, "mid": v(22.8, 9.76) * mm, "end": v(22.83, 9.46) * mm});
            skArc(sketch, "E7.67.0", {"start": v(21.07, 12.91) * mm, "mid": v(21.3, 12.7) * mm, "end": v(21.6, 12.65) * mm});
            skArc(sketch, "E7.67.1", {"start": v(21.6, 12.65) * mm, "mid": v(21.72, 12.67) * mm, "end": v(21.83, 12.7) * mm});
            skArc(sketch, "E7.67.2", {"start": v(22.13, 12.59) * mm, "mid": v(22, 12.7) * mm, "end": v(21.83, 12.7) * mm});
            skArc(sketch, "E7.67.3", {"start": v(22.3, 12.3) * mm, "mid": v(22.22, 12.44) * mm, "end": v(22.13, 12.59) * mm});
            skArc(sketch, "E7.67.4", {"start": v(22.24, 11.98) * mm, "mid": v(22.33, 12.12) * mm, "end": v(22.3, 12.3) * mm});
            skArc(sketch, "E7.67.5", {"start": v(22.24, 11.98) * mm, "mid": v(22.15, 11.9) * mm, "end": v(22.08, 11.81) * mm});
            skArc(sketch, "E7.67.6", {"start": v(22.08, 11.81) * mm, "mid": v(21.96, 11.52) * mm, "end": v(22.02, 11.22) * mm});
            skArc(sketch, "E7.68.0", {"start": v(20, 14.53) * mm, "mid": v(20.24, 14.34) * mm, "end": v(20.54, 14.3) * mm});
            skArc(sketch, "E7.68.1", {"start": v(20.54, 14.3) * mm, "mid": v(20.66, 14.34) * mm, "end": v(20.77, 14.38) * mm});
            skArc(sketch, "E7.68.2", {"start": v(21.08, 14.29) * mm, "mid": v(20.94, 14.39) * mm, "end": v(20.77, 14.38) * mm});
            skArc(sketch, "E7.68.3", {"start": v(21.26, 14) * mm, "mid": v(21.17, 14.15) * mm, "end": v(21.08, 14.29) * mm});
            skArc(sketch, "E7.68.4", {"start": v(21.23, 13.68) * mm, "mid": v(21.3, 13.84) * mm, "end": v(21.26, 14) * mm});
            skArc(sketch, "E7.68.5", {"start": v(21.23, 13.68) * mm, "mid": v(21.15, 13.6) * mm, "end": v(21.08, 13.5) * mm});
            skArc(sketch, "E7.68.6", {"start": v(21.08, 13.5) * mm, "mid": v(21, 13.21) * mm, "end": v(21.07, 12.91) * mm});
            skArc(sketch, "E7.69.0", {"start": v(18.8, 16.05) * mm, "mid": v(19.05, 15.88) * mm, "end": v(19.36, 15.88) * mm});
            skArc(sketch, "E7.69.1", {"start": v(19.36, 15.88) * mm, "mid": v(19.47, 15.91) * mm, "end": v(19.57, 15.96) * mm});
            skArc(sketch, "E7.69.2", {"start": v(19.9, 15.9) * mm, "mid": v(19.75, 15.99) * mm, "end": v(19.57, 15.96) * mm});
            skArc(sketch, "E7.69.3", {"start": v(20.1, 15.63) * mm, "mid": v(20, 15.76) * mm, "end": v(19.9, 15.9) * mm});
            skArc(sketch, "E7.69.4", {"start": v(20.09, 15.3) * mm, "mid": v(20.15, 15.47) * mm, "end": v(20.1, 15.63) * mm});
            skArc(sketch, "E7.69.5", {"start": v(20.09, 15.3) * mm, "mid": v(20.02, 15.22) * mm, "end": v(19.96, 15.12) * mm});
            skArc(sketch, "E7.69.6", {"start": v(19.96, 15.12) * mm, "mid": v(19.89, 14.82) * mm, "end": v(20, 14.53) * mm});
            skArc(sketch, "E7.70.0", {"start": v(17.48, 17.48) * mm, "mid": v(17.75, 17.33) * mm, "end": v(18.05, 17.35) * mm});
            skArc(sketch, "E7.70.1", {"start": v(18.05, 17.35) * mm, "mid": v(18.16, 17.4) * mm, "end": v(18.26, 17.45) * mm});
            skArc(sketch, "E7.70.2", {"start": v(18.58, 17.4) * mm, "mid": v(18.43, 17.49) * mm, "end": v(18.26, 17.45) * mm});
            skArc(sketch, "E7.70.3", {"start": v(18.81, 17.16) * mm, "mid": v(18.7, 17.28) * mm, "end": v(18.58, 17.4) * mm});
            skArc(sketch, "E7.70.4", {"start": v(18.83, 16.84) * mm, "mid": v(18.88, 17) * mm, "end": v(18.81, 17.16) * mm});
            skArc(sketch, "E7.70.5", {"start": v(18.83, 16.84) * mm, "mid": v(18.76, 16.74) * mm, "end": v(18.7, 16.64) * mm});
            skArc(sketch, "E7.70.6", {"start": v(18.7, 16.64) * mm, "mid": v(18.67, 16.33) * mm, "end": v(18.8, 16.05) * mm});
            skArc(sketch, "E7.71.0", {"start": v(16.05, 18.8) * mm, "mid": v(16.33, 18.67) * mm, "end": v(16.64, 18.7) * mm});
            skArc(sketch, "E7.71.1", {"start": v(16.64, 18.7) * mm, "mid": v(16.74, 18.76) * mm, "end": v(16.84, 18.83) * mm});
            skArc(sketch, "E7.71.2", {"start": v(17.16, 18.81) * mm, "mid": v(17, 18.88) * mm, "end": v(16.84, 18.83) * mm});
            skArc(sketch, "E7.71.3", {"start": v(17.4, 18.58) * mm, "mid": v(17.28, 18.7) * mm, "end": v(17.16, 18.81) * mm});
            skArc(sketch, "E7.71.4", {"start": v(17.45, 18.26) * mm, "mid": v(17.49, 18.43) * mm, "end": v(17.4, 18.58) * mm});
            skArc(sketch, "E7.71.5", {"start": v(17.45, 18.26) * mm, "mid": v(17.4, 18.16) * mm, "end": v(17.35, 18.05) * mm});
            skArc(sketch, "E7.71.6", {"start": v(17.35, 18.05) * mm, "mid": v(17.33, 17.75) * mm, "end": v(17.48, 17.48) * mm});
            skArc(sketch, "E7.72.0", {"start": v(14.53, 20) * mm, "mid": v(14.82, 19.89) * mm, "end": v(15.12, 19.96) * mm});
            skArc(sketch, "E7.72.1", {"start": v(15.12, 19.96) * mm, "mid": v(15.22, 20.02) * mm, "end": v(15.3, 20.09) * mm});
            skArc(sketch, "E7.72.2", {"start": v(15.63, 20.1) * mm, "mid": v(15.47, 20.15) * mm, "end": v(15.3, 20.09) * mm});
            skArc(sketch, "E7.72.3", {"start": v(15.9, 19.9) * mm, "mid": v(15.76, 20) * mm, "end": v(15.63, 20.1) * mm});
            skArc(sketch, "E7.72.4", {"start": v(15.96, 19.57) * mm, "mid": v(15.99, 19.75) * mm, "end": v(15.9, 19.9) * mm});
            skArc(sketch, "E7.72.5", {"start": v(15.96, 19.57) * mm, "mid": v(15.91, 19.47) * mm, "end": v(15.88, 19.36) * mm});
            skArc(sketch, "E7.72.6", {"start": v(15.88, 19.36) * mm, "mid": v(15.88, 19.05) * mm, "end": v(16.05, 18.8) * mm});
            skArc(sketch, "E7.73.0", {"start": v(12.91, 21.07) * mm, "mid": v(13.21, 21) * mm, "end": v(13.5, 21.08) * mm});
            skArc(sketch, "E7.73.1", {"start": v(13.5, 21.08) * mm, "mid": v(13.6, 21.15) * mm, "end": v(13.68, 21.23) * mm});
            skArc(sketch, "E7.73.2", {"start": v(14, 21.26) * mm, "mid": v(13.84, 21.3) * mm, "end": v(13.68, 21.23) * mm});
            skArc(sketch, "E7.73.3", {"start": v(14.29, 21.08) * mm, "mid": v(14.15, 21.17) * mm, "end": v(14, 21.26) * mm});
            skArc(sketch, "E7.73.4", {"start": v(14.38, 20.77) * mm, "mid": v(14.39, 20.94) * mm, "end": v(14.29, 21.08) * mm});
            skArc(sketch, "E7.73.5", {"start": v(14.38, 20.77) * mm, "mid": v(14.34, 20.66) * mm, "end": v(14.3, 20.54) * mm});
            skArc(sketch, "E7.73.6", {"start": v(14.3, 20.54) * mm, "mid": v(14.34, 20.24) * mm, "end": v(14.53, 20) * mm});
            skArc(sketch, "E7.74.0", {"start": v(11.22, 22.02) * mm, "mid": v(11.52, 21.96) * mm, "end": v(11.81, 22.08) * mm});
            skArc(sketch, "E7.74.1", {"start": v(11.81, 22.08) * mm, "mid": v(11.9, 22.15) * mm, "end": v(11.98, 22.24) * mm});
            skArc(sketch, "E7.74.2", {"start": v(12.3, 22.3) * mm, "mid": v(12.12, 22.33) * mm, "end": v(11.98, 22.24) * mm});
            skArc(sketch, "E7.74.3", {"start": v(12.59, 22.13) * mm, "mid": v(12.44, 22.22) * mm, "end": v(12.3, 22.3) * mm});
            skArc(sketch, "E7.74.4", {"start": v(12.7, 21.83) * mm, "mid": v(12.7, 22) * mm, "end": v(12.59, 22.13) * mm});
            skArc(sketch, "E7.74.5", {"start": v(12.7, 21.83) * mm, "mid": v(12.67, 21.72) * mm, "end": v(12.65, 21.6) * mm});
            skArc(sketch, "E7.74.6", {"start": v(12.65, 21.6) * mm, "mid": v(12.7, 21.3) * mm, "end": v(12.91, 21.07) * mm});
            skArc(sketch, "E7.75.0", {"start": v(9.46, 22.83) * mm, "mid": v(9.76, 22.8) * mm, "end": v(10.04, 22.93) * mm});
            skArc(sketch, "E7.75.1", {"start": v(10.04, 22.93) * mm, "mid": v(10.12, 23.02) * mm, "end": v(10.2, 23.1) * mm});
            skArc(sketch, "E7.75.2", {"start": v(10.5, 23.2) * mm, "mid": v(10.34, 23.2) * mm, "end": v(10.2, 23.1) * mm});
            skArc(sketch, "E7.75.3", {"start": v(10.81, 23.05) * mm, "mid": v(10.66, 23.12) * mm, "end": v(10.5, 23.2) * mm});
            skArc(sketch, "E7.75.4", {"start": v(10.95, 22.76) * mm, "mid": v(10.93, 22.93) * mm, "end": v(10.81, 23.05) * mm});
            skArc(sketch, "E7.75.5", {"start": v(10.95, 22.76) * mm, "mid": v(10.93, 22.65) * mm, "end": v(10.92, 22.53) * mm});
            skArc(sketch, "E7.75.6", {"start": v(10.92, 22.53) * mm, "mid": v(11, 22.23) * mm, "end": v(11.22, 22.02) * mm});
            skArc(sketch, "E7.76.0", {"start": v(7.64, 23.5) * mm, "mid": v(7.95, 23.5) * mm, "end": v(8.21, 23.65) * mm});
            skArc(sketch, "E7.76.1", {"start": v(8.21, 23.65) * mm, "mid": v(8.29, 23.74) * mm, "end": v(8.35, 23.84) * mm});
            skArc(sketch, "E7.76.2", {"start": v(8.66, 23.95) * mm, "mid": v(8.48, 23.95) * mm, "end": v(8.35, 23.84) * mm});
            skArc(sketch, "E7.76.3", {"start": v(8.97, 23.83) * mm, "mid": v(8.81, 23.89) * mm, "end": v(8.66, 23.95) * mm});
            skArc(sketch, "E7.76.4", {"start": v(9.13, 23.55) * mm, "mid": v(9.1, 23.72) * mm, "end": v(8.97, 23.83) * mm});
            skArc(sketch, "E7.76.5", {"start": v(9.13, 23.55) * mm, "mid": v(9.12, 23.43) * mm, "end": v(9.12, 23.32) * mm});
            skArc(sketch, "E7.76.6", {"start": v(9.12, 23.32) * mm, "mid": v(9.22, 23.03) * mm, "end": v(9.46, 22.83) * mm});
            skArc(sketch, "E7.77.0", {"start": v(5.77, 24.03) * mm, "mid": v(6.08, 24.05) * mm, "end": v(6.33, 24.22) * mm});
            skArc(sketch, "E7.77.1", {"start": v(6.33, 24.22) * mm, "mid": v(6.4, 24.32) * mm, "end": v(6.45, 24.42) * mm});
            skArc(sketch, "E7.77.2", {"start": v(6.75, 24.55) * mm, "mid": v(6.58, 24.54) * mm, "end": v(6.45, 24.42) * mm});
            skArc(sketch, "E7.77.3", {"start": v(7.07, 24.46) * mm, "mid": v(6.91, 24.5) * mm, "end": v(6.75, 24.55) * mm});
            skArc(sketch, "E7.77.4", {"start": v(7.26, 24.2) * mm, "mid": v(7.21, 24.36) * mm, "end": v(7.07, 24.46) * mm});
            skArc(sketch, "E7.77.5", {"start": v(7.26, 24.2) * mm, "mid": v(7.25, 24.08) * mm, "end": v(7.26, 23.96) * mm});
            skArc(sketch, "E7.77.6", {"start": v(7.26, 23.96) * mm, "mid": v(7.38, 23.68) * mm, "end": v(7.64, 23.5) * mm});
            skArc(sketch, "E7.78.0", {"start": v(3.87, 24.4) * mm, "mid": v(4.17, 24.45) * mm, "end": v(4.41, 24.64) * mm});
            skArc(sketch, "E7.78.1", {"start": v(4.41, 24.64) * mm, "mid": v(4.47, 24.74) * mm, "end": v(4.52, 24.85) * mm});
            skArc(sketch, "E7.78.2", {"start": v(4.8, 25) * mm, "mid": v(4.63, 24.98) * mm, "end": v(4.52, 24.85) * mm});
            skArc(sketch, "E7.78.3", {"start": v(5.13, 24.94) * mm, "mid": v(4.97, 24.97) * mm, "end": v(4.8, 25) * mm});
            skArc(sketch, "E7.78.4", {"start": v(5.33, 24.69) * mm, "mid": v(5.28, 24.85) * mm, "end": v(5.13, 24.94) * mm});
            skArc(sketch, "E7.78.5", {"start": v(5.33, 24.69) * mm, "mid": v(5.34, 24.57) * mm, "end": v(5.36, 24.46) * mm});
            skArc(sketch, "E7.78.6", {"start": v(5.36, 24.46) * mm, "mid": v(5.5, 24.18) * mm, "end": v(5.77, 24.03) * mm});
            skArc(sketch, "E7.79.0", {"start": v(1.94, 24.64) * mm, "mid": v(2.24, 24.7) * mm, "end": v(2.46, 24.91) * mm});
            skArc(sketch, "E7.79.1", {"start": v(2.46, 24.91) * mm, "mid": v(2.52, 25.02) * mm, "end": v(2.55, 25.13) * mm});
            skArc(sketch, "E7.79.2", {"start": v(2.83, 25.3) * mm, "mid": v(2.66, 25.27) * mm, "end": v(2.55, 25.13) * mm});
            skArc(sketch, "E7.79.3", {"start": v(3.16, 25.27) * mm, "mid": v(3, 25.29) * mm, "end": v(2.83, 25.3) * mm});
            skArc(sketch, "E7.79.4", {"start": v(3.38, 25.03) * mm, "mid": v(3.31, 25.19) * mm, "end": v(3.16, 25.27) * mm});
            skArc(sketch, "E7.79.5", {"start": v(3.38, 25.03) * mm, "mid": v(3.4, 24.91) * mm, "end": v(3.42, 24.8) * mm});
            skArc(sketch, "E7.79.6", {"start": v(3.42, 24.8) * mm, "mid": v(3.59, 24.54) * mm, "end": v(3.87, 24.4) * mm});
            skSolve(sketch);
        }
        {
            var Q0;
            Q0=makeQuery(id+"F0.imprint","IMPRINT",FACE,{"disambiguationData":[TD([[makeQuery(id+"F0.imprint","IMPRINT",EDGE,{"derivedFrom":sQuery(id+"F0.wireOp",EDGE,"E0")}),-1.0]])]});
            extrude(context, id + "F1", {"entities" : qUnion([Q0]), "depth" : 6.35 * mm, "offsetDistance" : 25.4 * mm});
        }
        {
            var Q0;
            Q0=makeQuery(id+"F1.opExtrude","CAP_FACE",FACE,{"disambiguationData":[OSD([sQuery(id+"F0.wireOp",EDGE,"E0"),sQuery(id+"F0.wireOp",EDGE,"E1"),sQuery(id+"F0.wireOp",EDGE,"E2"),sQuery(id+"F0.wireOp",EDGE,"E3"),sQuery(id+"F0.wireOp",EDGE,"E4.trimOffspring"),sQuery(id+"F0.wireOp",EDGE,"E5.filletArc"),sQuery(id+"F0.wireOp",EDGE,"E6.filletArc"),sQuery(id+"F0.wireOp",EDGE,"E7.1.0"),sQuery(id+"F0.wireOp",EDGE,"E7.1.1"),sQuery(id+"F0.wireOp",EDGE,"E7.1.2"),sQuery(id+"F0.wireOp",EDGE,"E7.1.3"),sQuery(id+"F0.wireOp",EDGE,"E7.1.4"),sQuery(id+"F0.wireOp",EDGE,"E7.1.5"),sQuery(id+"F0.wireOp",EDGE,"E7.1.6"),sQuery(id+"F0.wireOp",EDGE,"E7.2.0"),sQuery(id+"F0.wireOp",EDGE,"E7.2.1"),sQuery(id+"F0.wireOp",EDGE,"E7.2.2"),sQuery(id+"F0.wireOp",EDGE,"E7.2.3"),sQuery(id+"F0.wireOp",EDGE,"E7.2.4"),sQuery(id+"F0.wireOp",EDGE,"E7.2.5"),sQuery(id+"F0.wireOp",EDGE,"E7.2.6"),sQuery(id+"F0.wireOp",EDGE,"E7.3.0"),sQuery(id+"F0.wireOp",EDGE,"E7.3.1"),sQuery(id+"F0.wireOp",EDGE,"E7.3.2"),sQuery(id+"F0.wireOp",EDGE,"E7.3.3"),sQuery(id+"F0.wireOp",EDGE,"E7.3.4"),sQuery(id+"F0.wireOp",EDGE,"E7.3.5"),sQuery(id+"F0.wireOp",EDGE,"E7.3.6"),sQuery(id+"F0.wireOp",EDGE,"E7.4.0"),sQuery(id+"F0.wireOp",EDGE,"E7.4.1"),sQuery(id+"F0.wireOp",EDGE,"E7.4.2"),sQuery(id+"F0.wireOp",EDGE,"E7.4.3"),sQuery(id+"F0.wireOp",EDGE,"E7.4.4"),sQuery(id+"F0.wireOp",EDGE,"E7.4.5"),sQuery(id+"F0.wireOp",EDGE,"E7.4.6"),sQuery(id+"F0.wireOp",EDGE,"E7.5.0"),sQuery(id+"F0.wireOp",EDGE,"E7.5.1"),sQuery(id+"F0.wireOp",EDGE,"E7.5.2"),sQuery(id+"F0.wireOp",EDGE,"E7.5.3"),sQuery(id+"F0.wireOp",EDGE,"E7.5.4"),sQuery(id+"F0.wireOp",EDGE,"E7.5.5"),sQuery(id+"F0.wireOp",EDGE,"E7.5.6"),sQuery(id+"F0.wireOp",EDGE,"E7.6.0"),sQuery(id+"F0.wireOp",EDGE,"E7.6.1"),sQuery(id+"F0.wireOp",EDGE,"E7.6.2"),sQuery(id+"F0.wireOp",EDGE,"E7.6.3"),sQuery(id+"F0.wireOp",EDGE,"E7.6.4"),sQuery(id+"F0.wireOp",EDGE,"E7.6.5"),sQuery(id+"F0.wireOp",EDGE,"E7.6.6"),sQuery(id+"F0.wireOp",EDGE,"E7.7.0"),sQuery(id+"F0.wireOp",EDGE,"E7.7.1"),sQuery(id+"F0.wireOp",EDGE,"E7.7.2"),sQuery(id+"F0.wireOp",EDGE,"E7.7.3"),sQuery(id+"F0.wireOp",EDGE,"E7.7.4"),sQuery(id+"F0.wireOp",EDGE,"E7.7.5"),sQuery(id+"F0.wireOp",EDGE,"E7.7.6"),sQuery(id+"F0.wireOp",EDGE,"E7.8.0"),sQuery(id+"F0.wireOp",EDGE,"E7.8.1"),sQuery(id+"F0.wireOp",EDGE,"E7.8.2"),sQuery(id+"F0.wireOp",EDGE,"E7.8.3"),sQuery(id+"F0.wireOp",EDGE,"E7.8.4"),sQuery(id+"F0.wireOp",EDGE,"E7.8.5"),sQuery(id+"F0.wireOp",EDGE,"E7.8.6"),sQuery(id+"F0.wireOp",EDGE,"E7.9.0"),sQuery(id+"F0.wireOp",EDGE,"E7.9.1"),sQuery(id+"F0.wireOp",EDGE,"E7.9.2"),sQuery(id+"F0.wireOp",EDGE,"E7.9.3"),sQuery(id+"F0.wireOp",EDGE,"E7.9.4"),sQuery(id+"F0.wireOp",EDGE,"E7.9.5"),sQuery(id+"F0.wireOp",EDGE,"E7.9.6"),sQuery(id+"F0.wireOp",EDGE,"E7.10.0"),sQuery(id+"F0.wireOp",EDGE,"E7.10.1"),sQuery(id+"F0.wireOp",EDGE,"E7.10.2"),sQuery(id+"F0.wireOp",EDGE,"E7.10.3"),sQuery(id+"F0.wireOp",EDGE,"E7.10.4"),sQuery(id+"F0.wireOp",EDGE,"E7.10.5"),sQuery(id+"F0.wireOp",EDGE,"E7.10.6"),sQuery(id+"F0.wireOp",EDGE,"E7.11.0"),sQuery(id+"F0.wireOp",EDGE,"E7.11.1"),sQuery(id+"F0.wireOp",EDGE,"E7.11.2"),sQuery(id+"F0.wireOp",EDGE,"E7.11.3"),sQuery(id+"F0.wireOp",EDGE,"E7.11.4"),sQuery(id+"F0.wireOp",EDGE,"E7.11.5"),sQuery(id+"F0.wireOp",EDGE,"E7.11.6"),sQuery(id+"F0.wireOp",EDGE,"E7.12.0"),sQuery(id+"F0.wireOp",EDGE,"E7.12.1"),sQuery(id+"F0.wireOp",EDGE,"E7.12.2"),sQuery(id+"F0.wireOp",EDGE,"E7.12.3"),sQuery(id+"F0.wireOp",EDGE,"E7.12.4"),sQuery(id+"F0.wireOp",EDGE,"E7.12.5"),sQuery(id+"F0.wireOp",EDGE,"E7.12.6"),sQuery(id+"F0.wireOp",EDGE,"E7.13.0"),sQuery(id+"F0.wireOp",EDGE,"E7.13.1"),sQuery(id+"F0.wireOp",EDGE,"E7.13.2"),sQuery(id+"F0.wireOp",EDGE,"E7.13.3"),sQuery(id+"F0.wireOp",EDGE,"E7.13.4"),sQuery(id+"F0.wireOp",EDGE,"E7.13.5"),sQuery(id+"F0.wireOp",EDGE,"E7.13.6"),sQuery(id+"F0.wireOp",EDGE,"E7.14.0"),sQuery(id+"F0.wireOp",EDGE,"E7.14.1"),sQuery(id+"F0.wireOp",EDGE,"E7.14.2"),sQuery(id+"F0.wireOp",EDGE,"E7.14.3"),sQuery(id+"F0.wireOp",EDGE,"E7.14.4"),sQuery(id+"F0.wireOp",EDGE,"E7.14.5"),sQuery(id+"F0.wireOp",EDGE,"E7.14.6"),sQuery(id+"F0.wireOp",EDGE,"E7.15.0"),sQuery(id+"F0.wireOp",EDGE,"E7.15.1"),sQuery(id+"F0.wireOp",EDGE,"E7.15.2"),sQuery(id+"F0.wireOp",EDGE,"E7.15.3"),sQuery(id+"F0.wireOp",EDGE,"E7.15.4"),sQuery(id+"F0.wireOp",EDGE,"E7.15.5"),sQuery(id+"F0.wireOp",EDGE,"E7.15.6"),sQuery(id+"F0.wireOp",EDGE,"E7.16.0"),sQuery(id+"F0.wireOp",EDGE,"E7.16.1"),sQuery(id+"F0.wireOp",EDGE,"E7.16.2"),sQuery(id+"F0.wireOp",EDGE,"E7.16.3"),sQuery(id+"F0.wireOp",EDGE,"E7.16.4"),sQuery(id+"F0.wireOp",EDGE,"E7.16.5"),sQuery(id+"F0.wireOp",EDGE,"E7.16.6"),sQuery(id+"F0.wireOp",EDGE,"E7.17.0"),sQuery(id+"F0.wireOp",EDGE,"E7.17.1"),sQuery(id+"F0.wireOp",EDGE,"E7.17.2"),sQuery(id+"F0.wireOp",EDGE,"E7.17.3"),sQuery(id+"F0.wireOp",EDGE,"E7.17.4"),sQuery(id+"F0.wireOp",EDGE,"E7.17.5"),sQuery(id+"F0.wireOp",EDGE,"E7.17.6"),sQuery(id+"F0.wireOp",EDGE,"E7.18.0"),sQuery(id+"F0.wireOp",EDGE,"E7.18.1"),sQuery(id+"F0.wireOp",EDGE,"E7.18.2"),sQuery(id+"F0.wireOp",EDGE,"E7.18.3"),sQuery(id+"F0.wireOp",EDGE,"E7.18.4"),sQuery(id+"F0.wireOp",EDGE,"E7.18.5"),sQuery(id+"F0.wireOp",EDGE,"E7.18.6"),sQuery(id+"F0.wireOp",EDGE,"E7.19.0"),sQuery(id+"F0.wireOp",EDGE,"E7.19.1"),sQuery(id+"F0.wireOp",EDGE,"E7.19.2"),sQuery(id+"F0.wireOp",EDGE,"E7.19.3"),sQuery(id+"F0.wireOp",EDGE,"E7.19.4"),sQuery(id+"F0.wireOp",EDGE,"E7.19.5"),sQuery(id+"F0.wireOp",EDGE,"E7.19.6"),sQuery(id+"F0.wireOp",EDGE,"E7.20.0"),sQuery(id+"F0.wireOp",EDGE,"E7.20.1"),sQuery(id+"F0.wireOp",EDGE,"E7.20.2"),sQuery(id+"F0.wireOp",EDGE,"E7.20.3"),sQuery(id+"F0.wireOp",EDGE,"E7.20.4"),sQuery(id+"F0.wireOp",EDGE,"E7.20.5"),sQuery(id+"F0.wireOp",EDGE,"E7.20.6"),sQuery(id+"F0.wireOp",EDGE,"E7.21.0"),sQuery(id+"F0.wireOp",EDGE,"E7.21.1"),sQuery(id+"F0.wireOp",EDGE,"E7.21.2"),sQuery(id+"F0.wireOp",EDGE,"E7.21.3"),sQuery(id+"F0.wireOp",EDGE,"E7.21.4"),sQuery(id+"F0.wireOp",EDGE,"E7.21.5"),sQuery(id+"F0.wireOp",EDGE,"E7.21.6"),sQuery(id+"F0.wireOp",EDGE,"E7.22.0"),sQuery(id+"F0.wireOp",EDGE,"E7.22.1"),sQuery(id+"F0.wireOp",EDGE,"E7.22.2"),sQuery(id+"F0.wireOp",EDGE,"E7.22.3"),sQuery(id+"F0.wireOp",EDGE,"E7.22.4"),sQuery(id+"F0.wireOp",EDGE,"E7.22.5"),sQuery(id+"F0.wireOp",EDGE,"E7.22.6"),sQuery(id+"F0.wireOp",EDGE,"E7.23.0"),sQuery(id+"F0.wireOp",EDGE,"E7.23.1"),sQuery(id+"F0.wireOp",EDGE,"E7.23.2"),sQuery(id+"F0.wireOp",EDGE,"E7.23.3"),sQuery(id+"F0.wireOp",EDGE,"E7.23.4"),sQuery(id+"F0.wireOp",EDGE,"E7.23.5"),sQuery(id+"F0.wireOp",EDGE,"E7.23.6"),sQuery(id+"F0.wireOp",EDGE,"E7.24.0"),sQuery(id+"F0.wireOp",EDGE,"E7.24.1"),sQuery(id+"F0.wireOp",EDGE,"E7.24.2"),sQuery(id+"F0.wireOp",EDGE,"E7.24.3"),sQuery(id+"F0.wireOp",EDGE,"E7.24.4"),sQuery(id+"F0.wireOp",EDGE,"E7.24.5"),sQuery(id+"F0.wireOp",EDGE,"E7.24.6"),sQuery(id+"F0.wireOp",EDGE,"E7.25.0"),sQuery(id+"F0.wireOp",EDGE,"E7.25.1"),sQuery(id+"F0.wireOp",EDGE,"E7.25.2"),sQuery(id+"F0.wireOp",EDGE,"E7.25.3"),sQuery(id+"F0.wireOp",EDGE,"E7.25.4"),sQuery(id+"F0.wireOp",EDGE,"E7.25.5"),sQuery(id+"F0.wireOp",EDGE,"E7.25.6"),sQuery(id+"F0.wireOp",EDGE,"E7.26.0"),sQuery(id+"F0.wireOp",EDGE,"E7.26.1"),sQuery(id+"F0.wireOp",EDGE,"E7.26.2"),sQuery(id+"F0.wireOp",EDGE,"E7.26.3"),sQuery(id+"F0.wireOp",EDGE,"E7.26.4"),sQuery(id+"F0.wireOp",EDGE,"E7.26.5"),sQuery(id+"F0.wireOp",EDGE,"E7.26.6"),sQuery(id+"F0.wireOp",EDGE,"E7.27.0"),sQuery(id+"F0.wireOp",EDGE,"E7.27.1"),sQuery(id+"F0.wireOp",EDGE,"E7.27.2"),sQuery(id+"F0.wireOp",EDGE,"E7.27.3"),sQuery(id+"F0.wireOp",EDGE,"E7.27.4"),sQuery(id+"F0.wireOp",EDGE,"E7.27.5"),sQuery(id+"F0.wireOp",EDGE,"E7.27.6"),sQuery(id+"F0.wireOp",EDGE,"E7.28.0"),sQuery(id+"F0.wireOp",EDGE,"E7.28.1"),sQuery(id+"F0.wireOp",EDGE,"E7.28.2"),sQuery(id+"F0.wireOp",EDGE,"E7.28.3"),sQuery(id+"F0.wireOp",EDGE,"E7.28.4"),sQuery(id+"F0.wireOp",EDGE,"E7.28.5"),sQuery(id+"F0.wireOp",EDGE,"E7.28.6"),sQuery(id+"F0.wireOp",EDGE,"E7.29.0"),sQuery(id+"F0.wireOp",EDGE,"E7.29.1"),sQuery(id+"F0.wireOp",EDGE,"E7.29.2"),sQuery(id+"F0.wireOp",EDGE,"E7.29.3"),sQuery(id+"F0.wireOp",EDGE,"E7.29.4"),sQuery(id+"F0.wireOp",EDGE,"E7.29.5"),sQuery(id+"F0.wireOp",EDGE,"E7.29.6"),sQuery(id+"F0.wireOp",EDGE,"E7.30.0"),sQuery(id+"F0.wireOp",EDGE,"E7.30.1"),sQuery(id+"F0.wireOp",EDGE,"E7.30.2"),sQuery(id+"F0.wireOp",EDGE,"E7.30.3"),sQuery(id+"F0.wireOp",EDGE,"E7.30.4"),sQuery(id+"F0.wireOp",EDGE,"E7.30.5"),sQuery(id+"F0.wireOp",EDGE,"E7.30.6"),sQuery(id+"F0.wireOp",EDGE,"E7.31.0"),sQuery(id+"F0.wireOp",EDGE,"E7.31.1"),sQuery(id+"F0.wireOp",EDGE,"E7.31.2"),sQuery(id+"F0.wireOp",EDGE,"E7.31.3"),sQuery(id+"F0.wireOp",EDGE,"E7.31.4"),sQuery(id+"F0.wireOp",EDGE,"E7.31.5"),sQuery(id+"F0.wireOp",EDGE,"E7.31.6"),sQuery(id+"F0.wireOp",EDGE,"E7.32.0"),sQuery(id+"F0.wireOp",EDGE,"E7.32.1"),sQuery(id+"F0.wireOp",EDGE,"E7.32.2"),sQuery(id+"F0.wireOp",EDGE,"E7.32.3"),sQuery(id+"F0.wireOp",EDGE,"E7.32.4"),sQuery(id+"F0.wireOp",EDGE,"E7.32.5"),sQuery(id+"F0.wireOp",EDGE,"E7.32.6"),sQuery(id+"F0.wireOp",EDGE,"E7.33.0"),sQuery(id+"F0.wireOp",EDGE,"E7.33.1"),sQuery(id+"F0.wireOp",EDGE,"E7.33.2"),sQuery(id+"F0.wireOp",EDGE,"E7.33.3"),sQuery(id+"F0.wireOp",EDGE,"E7.33.4"),sQuery(id+"F0.wireOp",EDGE,"E7.33.5"),sQuery(id+"F0.wireOp",EDGE,"E7.33.6"),sQuery(id+"F0.wireOp",EDGE,"E7.34.0"),sQuery(id+"F0.wireOp",EDGE,"E7.34.1"),sQuery(id+"F0.wireOp",EDGE,"E7.34.2"),sQuery(id+"F0.wireOp",EDGE,"E7.34.3"),sQuery(id+"F0.wireOp",EDGE,"E7.34.4"),sQuery(id+"F0.wireOp",EDGE,"E7.34.5"),sQuery(id+"F0.wireOp",EDGE,"E7.34.6"),sQuery(id+"F0.wireOp",EDGE,"E7.35.0"),sQuery(id+"F0.wireOp",EDGE,"E7.35.1"),sQuery(id+"F0.wireOp",EDGE,"E7.35.2"),sQuery(id+"F0.wireOp",EDGE,"E7.35.3"),sQuery(id+"F0.wireOp",EDGE,"E7.35.4"),sQuery(id+"F0.wireOp",EDGE,"E7.35.5"),sQuery(id+"F0.wireOp",EDGE,"E7.35.6"),sQuery(id+"F0.wireOp",EDGE,"E7.36.0"),sQuery(id+"F0.wireOp",EDGE,"E7.36.1"),sQuery(id+"F0.wireOp",EDGE,"E7.36.2"),sQuery(id+"F0.wireOp",EDGE,"E7.36.3"),sQuery(id+"F0.wireOp",EDGE,"E7.36.4"),sQuery(id+"F0.wireOp",EDGE,"E7.36.5"),sQuery(id+"F0.wireOp",EDGE,"E7.36.6"),sQuery(id+"F0.wireOp",EDGE,"E7.37.0"),sQuery(id+"F0.wireOp",EDGE,"E7.37.1"),sQuery(id+"F0.wireOp",EDGE,"E7.37.2"),sQuery(id+"F0.wireOp",EDGE,"E7.37.3"),sQuery(id+"F0.wireOp",EDGE,"E7.37.4"),sQuery(id+"F0.wireOp",EDGE,"E7.37.5"),sQuery(id+"F0.wireOp",EDGE,"E7.37.6"),sQuery(id+"F0.wireOp",EDGE,"E7.38.0"),sQuery(id+"F0.wireOp",EDGE,"E7.38.1"),sQuery(id+"F0.wireOp",EDGE,"E7.38.2"),sQuery(id+"F0.wireOp",EDGE,"E7.38.3"),sQuery(id+"F0.wireOp",EDGE,"E7.38.4"),sQuery(id+"F0.wireOp",EDGE,"E7.38.5"),sQuery(id+"F0.wireOp",EDGE,"E7.38.6"),sQuery(id+"F0.wireOp",EDGE,"E7.39.0"),sQuery(id+"F0.wireOp",EDGE,"E7.39.1"),sQuery(id+"F0.wireOp",EDGE,"E7.39.2"),sQuery(id+"F0.wireOp",EDGE,"E7.39.3"),sQuery(id+"F0.wireOp",EDGE,"E7.39.4"),sQuery(id+"F0.wireOp",EDGE,"E7.39.5"),sQuery(id+"F0.wireOp",EDGE,"E7.39.6"),sQuery(id+"F0.wireOp",EDGE,"E7.40.0"),sQuery(id+"F0.wireOp",EDGE,"E7.40.1"),sQuery(id+"F0.wireOp",EDGE,"E7.40.2"),sQuery(id+"F0.wireOp",EDGE,"E7.40.3"),sQuery(id+"F0.wireOp",EDGE,"E7.40.4"),sQuery(id+"F0.wireOp",EDGE,"E7.40.5"),sQuery(id+"F0.wireOp",EDGE,"E7.40.6"),sQuery(id+"F0.wireOp",EDGE,"E7.41.0"),sQuery(id+"F0.wireOp",EDGE,"E7.41.1"),sQuery(id+"F0.wireOp",EDGE,"E7.41.2"),sQuery(id+"F0.wireOp",EDGE,"E7.41.3"),sQuery(id+"F0.wireOp",EDGE,"E7.41.4"),sQuery(id+"F0.wireOp",EDGE,"E7.41.5"),sQuery(id+"F0.wireOp",EDGE,"E7.41.6"),sQuery(id+"F0.wireOp",EDGE,"E7.42.0"),sQuery(id+"F0.wireOp",EDGE,"E7.42.1"),sQuery(id+"F0.wireOp",EDGE,"E7.42.2"),sQuery(id+"F0.wireOp",EDGE,"E7.42.3"),sQuery(id+"F0.wireOp",EDGE,"E7.42.4"),sQuery(id+"F0.wireOp",EDGE,"E7.42.5"),sQuery(id+"F0.wireOp",EDGE,"E7.42.6"),sQuery(id+"F0.wireOp",EDGE,"E7.43.0"),sQuery(id+"F0.wireOp",EDGE,"E7.43.1"),sQuery(id+"F0.wireOp",EDGE,"E7.43.2"),sQuery(id+"F0.wireOp",EDGE,"E7.43.3"),sQuery(id+"F0.wireOp",EDGE,"E7.43.4"),sQuery(id+"F0.wireOp",EDGE,"E7.43.5"),sQuery(id+"F0.wireOp",EDGE,"E7.43.6"),sQuery(id+"F0.wireOp",EDGE,"E7.44.0"),sQuery(id+"F0.wireOp",EDGE,"E7.44.1"),sQuery(id+"F0.wireOp",EDGE,"E7.44.2"),sQuery(id+"F0.wireOp",EDGE,"E7.44.3"),sQuery(id+"F0.wireOp",EDGE,"E7.44.4"),sQuery(id+"F0.wireOp",EDGE,"E7.44.5"),sQuery(id+"F0.wireOp",EDGE,"E7.44.6"),sQuery(id+"F0.wireOp",EDGE,"E7.45.0"),sQuery(id+"F0.wireOp",EDGE,"E7.45.1"),sQuery(id+"F0.wireOp",EDGE,"E7.45.2"),sQuery(id+"F0.wireOp",EDGE,"E7.45.3"),sQuery(id+"F0.wireOp",EDGE,"E7.45.4"),sQuery(id+"F0.wireOp",EDGE,"E7.45.5"),sQuery(id+"F0.wireOp",EDGE,"E7.45.6"),sQuery(id+"F0.wireOp",EDGE,"E7.46.0"),sQuery(id+"F0.wireOp",EDGE,"E7.46.1"),sQuery(id+"F0.wireOp",EDGE,"E7.46.2"),sQuery(id+"F0.wireOp",EDGE,"E7.46.3"),sQuery(id+"F0.wireOp",EDGE,"E7.46.4"),sQuery(id+"F0.wireOp",EDGE,"E7.46.5"),sQuery(id+"F0.wireOp",EDGE,"E7.46.6"),sQuery(id+"F0.wireOp",EDGE,"E7.47.0"),sQuery(id+"F0.wireOp",EDGE,"E7.47.1"),sQuery(id+"F0.wireOp",EDGE,"E7.47.2"),sQuery(id+"F0.wireOp",EDGE,"E7.47.3"),sQuery(id+"F0.wireOp",EDGE,"E7.47.4"),sQuery(id+"F0.wireOp",EDGE,"E7.47.5"),sQuery(id+"F0.wireOp",EDGE,"E7.47.6"),sQuery(id+"F0.wireOp",EDGE,"E7.48.0"),sQuery(id+"F0.wireOp",EDGE,"E7.48.1"),sQuery(id+"F0.wireOp",EDGE,"E7.48.2"),sQuery(id+"F0.wireOp",EDGE,"E7.48.3"),sQuery(id+"F0.wireOp",EDGE,"E7.48.4"),sQuery(id+"F0.wireOp",EDGE,"E7.48.5"),sQuery(id+"F0.wireOp",EDGE,"E7.48.6"),sQuery(id+"F0.wireOp",EDGE,"E7.49.0"),sQuery(id+"F0.wireOp",EDGE,"E7.49.1"),sQuery(id+"F0.wireOp",EDGE,"E7.49.2"),sQuery(id+"F0.wireOp",EDGE,"E7.49.3"),sQuery(id+"F0.wireOp",EDGE,"E7.49.4"),sQuery(id+"F0.wireOp",EDGE,"E7.49.5"),sQuery(id+"F0.wireOp",EDGE,"E7.49.6"),sQuery(id+"F0.wireOp",EDGE,"E7.50.0"),sQuery(id+"F0.wireOp",EDGE,"E7.50.1"),sQuery(id+"F0.wireOp",EDGE,"E7.50.2"),sQuery(id+"F0.wireOp",EDGE,"E7.50.3"),sQuery(id+"F0.wireOp",EDGE,"E7.50.4"),sQuery(id+"F0.wireOp",EDGE,"E7.50.5"),sQuery(id+"F0.wireOp",EDGE,"E7.50.6"),sQuery(id+"F0.wireOp",EDGE,"E7.51.0"),sQuery(id+"F0.wireOp",EDGE,"E7.51.1"),sQuery(id+"F0.wireOp",EDGE,"E7.51.2"),sQuery(id+"F0.wireOp",EDGE,"E7.51.3"),sQuery(id+"F0.wireOp",EDGE,"E7.51.4"),sQuery(id+"F0.wireOp",EDGE,"E7.51.5"),sQuery(id+"F0.wireOp",EDGE,"E7.51.6"),sQuery(id+"F0.wireOp",EDGE,"E7.52.0"),sQuery(id+"F0.wireOp",EDGE,"E7.52.1"),sQuery(id+"F0.wireOp",EDGE,"E7.52.2"),sQuery(id+"F0.wireOp",EDGE,"E7.52.3"),sQuery(id+"F0.wireOp",EDGE,"E7.52.4"),sQuery(id+"F0.wireOp",EDGE,"E7.52.5"),sQuery(id+"F0.wireOp",EDGE,"E7.52.6"),sQuery(id+"F0.wireOp",EDGE,"E7.53.0"),sQuery(id+"F0.wireOp",EDGE,"E7.53.1"),sQuery(id+"F0.wireOp",EDGE,"E7.53.2"),sQuery(id+"F0.wireOp",EDGE,"E7.53.3"),sQuery(id+"F0.wireOp",EDGE,"E7.53.4"),sQuery(id+"F0.wireOp",EDGE,"E7.53.5"),sQuery(id+"F0.wireOp",EDGE,"E7.53.6"),sQuery(id+"F0.wireOp",EDGE,"E7.54.0"),sQuery(id+"F0.wireOp",EDGE,"E7.54.1"),sQuery(id+"F0.wireOp",EDGE,"E7.54.2"),sQuery(id+"F0.wireOp",EDGE,"E7.54.3"),sQuery(id+"F0.wireOp",EDGE,"E7.54.4"),sQuery(id+"F0.wireOp",EDGE,"E7.54.5"),sQuery(id+"F0.wireOp",EDGE,"E7.54.6"),sQuery(id+"F0.wireOp",EDGE,"E7.55.0"),sQuery(id+"F0.wireOp",EDGE,"E7.55.1"),sQuery(id+"F0.wireOp",EDGE,"E7.55.2"),sQuery(id+"F0.wireOp",EDGE,"E7.55.3"),sQuery(id+"F0.wireOp",EDGE,"E7.55.4"),sQuery(id+"F0.wireOp",EDGE,"E7.55.5"),sQuery(id+"F0.wireOp",EDGE,"E7.55.6"),sQuery(id+"F0.wireOp",EDGE,"E7.56.0"),sQuery(id+"F0.wireOp",EDGE,"E7.56.1"),sQuery(id+"F0.wireOp",EDGE,"E7.56.2"),sQuery(id+"F0.wireOp",EDGE,"E7.56.3"),sQuery(id+"F0.wireOp",EDGE,"E7.56.4"),sQuery(id+"F0.wireOp",EDGE,"E7.56.5"),sQuery(id+"F0.wireOp",EDGE,"E7.56.6"),sQuery(id+"F0.wireOp",EDGE,"E7.57.0"),sQuery(id+"F0.wireOp",EDGE,"E7.57.1"),sQuery(id+"F0.wireOp",EDGE,"E7.57.2"),sQuery(id+"F0.wireOp",EDGE,"E7.57.3"),sQuery(id+"F0.wireOp",EDGE,"E7.57.4"),sQuery(id+"F0.wireOp",EDGE,"E7.57.5"),sQuery(id+"F0.wireOp",EDGE,"E7.57.6"),sQuery(id+"F0.wireOp",EDGE,"E7.58.0"),sQuery(id+"F0.wireOp",EDGE,"E7.58.1"),sQuery(id+"F0.wireOp",EDGE,"E7.58.2"),sQuery(id+"F0.wireOp",EDGE,"E7.58.3"),sQuery(id+"F0.wireOp",EDGE,"E7.58.4"),sQuery(id+"F0.wireOp",EDGE,"E7.58.5"),sQuery(id+"F0.wireOp",EDGE,"E7.58.6"),sQuery(id+"F0.wireOp",EDGE,"E7.59.0"),sQuery(id+"F0.wireOp",EDGE,"E7.59.1"),sQuery(id+"F0.wireOp",EDGE,"E7.59.2"),sQuery(id+"F0.wireOp",EDGE,"E7.59.3"),sQuery(id+"F0.wireOp",EDGE,"E7.59.4"),sQuery(id+"F0.wireOp",EDGE,"E7.59.5"),sQuery(id+"F0.wireOp",EDGE,"E7.59.6"),sQuery(id+"F0.wireOp",EDGE,"E7.60.0"),sQuery(id+"F0.wireOp",EDGE,"E7.60.1"),sQuery(id+"F0.wireOp",EDGE,"E7.60.2"),sQuery(id+"F0.wireOp",EDGE,"E7.60.3"),sQuery(id+"F0.wireOp",EDGE,"E7.60.4"),sQuery(id+"F0.wireOp",EDGE,"E7.60.5"),sQuery(id+"F0.wireOp",EDGE,"E7.60.6"),sQuery(id+"F0.wireOp",EDGE,"E7.61.0"),sQuery(id+"F0.wireOp",EDGE,"E7.61.1"),sQuery(id+"F0.wireOp",EDGE,"E7.61.2"),sQuery(id+"F0.wireOp",EDGE,"E7.61.3"),sQuery(id+"F0.wireOp",EDGE,"E7.61.4"),sQuery(id+"F0.wireOp",EDGE,"E7.61.5"),sQuery(id+"F0.wireOp",EDGE,"E7.61.6"),sQuery(id+"F0.wireOp",EDGE,"E7.62.0"),sQuery(id+"F0.wireOp",EDGE,"E7.62.1"),sQuery(id+"F0.wireOp",EDGE,"E7.62.2"),sQuery(id+"F0.wireOp",EDGE,"E7.62.3"),sQuery(id+"F0.wireOp",EDGE,"E7.62.4"),sQuery(id+"F0.wireOp",EDGE,"E7.62.5"),sQuery(id+"F0.wireOp",EDGE,"E7.62.6"),sQuery(id+"F0.wireOp",EDGE,"E7.63.0"),sQuery(id+"F0.wireOp",EDGE,"E7.63.1"),sQuery(id+"F0.wireOp",EDGE,"E7.63.2"),sQuery(id+"F0.wireOp",EDGE,"E7.63.3"),sQuery(id+"F0.wireOp",EDGE,"E7.63.4"),sQuery(id+"F0.wireOp",EDGE,"E7.63.5"),sQuery(id+"F0.wireOp",EDGE,"E7.63.6"),sQuery(id+"F0.wireOp",EDGE,"E7.64.0"),sQuery(id+"F0.wireOp",EDGE,"E7.64.1"),sQuery(id+"F0.wireOp",EDGE,"E7.64.2"),sQuery(id+"F0.wireOp",EDGE,"E7.64.3"),sQuery(id+"F0.wireOp",EDGE,"E7.64.4"),sQuery(id+"F0.wireOp",EDGE,"E7.64.5"),sQuery(id+"F0.wireOp",EDGE,"E7.64.6"),sQuery(id+"F0.wireOp",EDGE,"E7.65.0"),sQuery(id+"F0.wireOp",EDGE,"E7.65.1"),sQuery(id+"F0.wireOp",EDGE,"E7.65.2"),sQuery(id+"F0.wireOp",EDGE,"E7.65.3"),sQuery(id+"F0.wireOp",EDGE,"E7.65.4"),sQuery(id+"F0.wireOp",EDGE,"E7.65.5"),sQuery(id+"F0.wireOp",EDGE,"E7.65.6"),sQuery(id+"F0.wireOp",EDGE,"E7.66.0"),sQuery(id+"F0.wireOp",EDGE,"E7.66.1"),sQuery(id+"F0.wireOp",EDGE,"E7.66.2"),sQuery(id+"F0.wireOp",EDGE,"E7.66.3"),sQuery(id+"F0.wireOp",EDGE,"E7.66.4"),sQuery(id+"F0.wireOp",EDGE,"E7.66.5"),sQuery(id+"F0.wireOp",EDGE,"E7.66.6"),sQuery(id+"F0.wireOp",EDGE,"E7.67.0"),sQuery(id+"F0.wireOp",EDGE,"E7.67.1"),sQuery(id+"F0.wireOp",EDGE,"E7.67.2"),sQuery(id+"F0.wireOp",EDGE,"E7.67.3"),sQuery(id+"F0.wireOp",EDGE,"E7.67.4"),sQuery(id+"F0.wireOp",EDGE,"E7.67.5"),sQuery(id+"F0.wireOp",EDGE,"E7.67.6"),sQuery(id+"F0.wireOp",EDGE,"E7.68.0"),sQuery(id+"F0.wireOp",EDGE,"E7.68.1"),sQuery(id+"F0.wireOp",EDGE,"E7.68.2"),sQuery(id+"F0.wireOp",EDGE,"E7.68.3"),sQuery(id+"F0.wireOp",EDGE,"E7.68.4"),sQuery(id+"F0.wireOp",EDGE,"E7.68.5"),sQuery(id+"F0.wireOp",EDGE,"E7.68.6"),sQuery(id+"F0.wireOp",EDGE,"E7.69.0"),sQuery(id+"F0.wireOp",EDGE,"E7.69.1"),sQuery(id+"F0.wireOp",EDGE,"E7.69.2"),sQuery(id+"F0.wireOp",EDGE,"E7.69.3"),sQuery(id+"F0.wireOp",EDGE,"E7.69.4"),sQuery(id+"F0.wireOp",EDGE,"E7.69.5"),sQuery(id+"F0.wireOp",EDGE,"E7.69.6"),sQuery(id+"F0.wireOp",EDGE,"E7.70.0"),sQuery(id+"F0.wireOp",EDGE,"E7.70.1"),sQuery(id+"F0.wireOp",EDGE,"E7.70.2"),sQuery(id+"F0.wireOp",EDGE,"E7.70.3"),sQuery(id+"F0.wireOp",EDGE,"E7.70.4"),sQuery(id+"F0.wireOp",EDGE,"E7.70.5"),sQuery(id+"F0.wireOp",EDGE,"E7.70.6"),sQuery(id+"F0.wireOp",EDGE,"E7.71.0"),sQuery(id+"F0.wireOp",EDGE,"E7.71.1"),sQuery(id+"F0.wireOp",EDGE,"E7.71.2"),sQuery(id+"F0.wireOp",EDGE,"E7.71.3"),sQuery(id+"F0.wireOp",EDGE,"E7.71.4"),sQuery(id+"F0.wireOp",EDGE,"E7.71.5"),sQuery(id+"F0.wireOp",EDGE,"E7.71.6"),sQuery(id+"F0.wireOp",EDGE,"E7.72.0"),sQuery(id+"F0.wireOp",EDGE,"E7.72.1"),sQuery(id+"F0.wireOp",EDGE,"E7.72.2"),sQuery(id+"F0.wireOp",EDGE,"E7.72.3"),sQuery(id+"F0.wireOp",EDGE,"E7.72.4"),sQuery(id+"F0.wireOp",EDGE,"E7.72.5"),sQuery(id+"F0.wireOp",EDGE,"E7.72.6"),sQuery(id+"F0.wireOp",EDGE,"E7.73.0"),sQuery(id+"F0.wireOp",EDGE,"E7.73.1"),sQuery(id+"F0.wireOp",EDGE,"E7.73.2"),sQuery(id+"F0.wireOp",EDGE,"E7.73.3"),sQuery(id+"F0.wireOp",EDGE,"E7.73.4"),sQuery(id+"F0.wireOp",EDGE,"E7.73.5"),sQuery(id+"F0.wireOp",EDGE,"E7.73.6"),sQuery(id+"F0.wireOp",EDGE,"E7.74.0"),sQuery(id+"F0.wireOp",EDGE,"E7.74.1"),sQuery(id+"F0.wireOp",EDGE,"E7.74.2"),sQuery(id+"F0.wireOp",EDGE,"E7.74.3"),sQuery(id+"F0.wireOp",EDGE,"E7.74.4"),sQuery(id+"F0.wireOp",EDGE,"E7.74.5"),sQuery(id+"F0.wireOp",EDGE,"E7.74.6"),sQuery(id+"F0.wireOp",EDGE,"E7.75.0"),sQuery(id+"F0.wireOp",EDGE,"E7.75.1"),sQuery(id+"F0.wireOp",EDGE,"E7.75.2"),sQuery(id+"F0.wireOp",EDGE,"E7.75.3"),sQuery(id+"F0.wireOp",EDGE,"E7.75.4"),sQuery(id+"F0.wireOp",EDGE,"E7.75.5"),sQuery(id+"F0.wireOp",EDGE,"E7.75.6"),sQuery(id+"F0.wireOp",EDGE,"E7.76.0"),sQuery(id+"F0.wireOp",EDGE,"E7.76.1"),sQuery(id+"F0.wireOp",EDGE,"E7.76.2"),sQuery(id+"F0.wireOp",EDGE,"E7.76.3"),sQuery(id+"F0.wireOp",EDGE,"E7.76.4"),sQuery(id+"F0.wireOp",EDGE,"E7.76.5"),sQuery(id+"F0.wireOp",EDGE,"E7.76.6"),sQuery(id+"F0.wireOp",EDGE,"E7.77.0"),sQuery(id+"F0.wireOp",EDGE,"E7.77.1"),sQuery(id+"F0.wireOp",EDGE,"E7.77.2"),sQuery(id+"F0.wireOp",EDGE,"E7.77.3"),sQuery(id+"F0.wireOp",EDGE,"E7.77.4"),sQuery(id+"F0.wireOp",EDGE,"E7.77.5"),sQuery(id+"F0.wireOp",EDGE,"E7.77.6"),sQuery(id+"F0.wireOp",EDGE,"E7.78.0"),sQuery(id+"F0.wireOp",EDGE,"E7.78.1"),sQuery(id+"F0.wireOp",EDGE,"E7.78.2"),sQuery(id+"F0.wireOp",EDGE,"E7.78.3"),sQuery(id+"F0.wireOp",EDGE,"E7.78.4"),sQuery(id+"F0.wireOp",EDGE,"E7.78.5"),sQuery(id+"F0.wireOp",EDGE,"E7.78.6"),sQuery(id+"F0.wireOp",EDGE,"E7.79.0"),sQuery(id+"F0.wireOp",EDGE,"E7.79.1"),sQuery(id+"F0.wireOp",EDGE,"E7.79.2"),sQuery(id+"F0.wireOp",EDGE,"E7.79.3"),sQuery(id+"F0.wireOp",EDGE,"E7.79.4"),sQuery(id+"F0.wireOp",EDGE,"E7.79.5"),sQuery(id+"F0.wireOp",EDGE,"E7.79.6")])],"isStart":false});
            var sketch = newSketch(context, id + "F2", { "sketchPlane" : qUnion([Q0])});
            skCircle(sketch, "E8", {"center": v(0, 0) * mm, "radius": 26.67 * mm});
            skSolve(sketch);
        }
        {
            var Q0;
            Q0 = qSketchRegion(id + "F2", true);
            extrude(context, id + "F3", {"entities" : qUnion([Q0]), "operationType" : NewBodyOperationType.ADD, "depth" : 1 * mm, "offsetDistance" : 25.4 * mm});
        }
        {
            var Q0;
            Q0=makeQuery(id+"F1.opExtrude","CAP_FACE",FACE,{"disambiguationData":[OSD([sQuery(id+"F0.wireOp",EDGE,"E0"),sQuery(id+"F0.wireOp",EDGE,"E1"),sQuery(id+"F0.wireOp",EDGE,"E2"),sQuery(id+"F0.wireOp",EDGE,"E3"),sQuery(id+"F0.wireOp",EDGE,"E4.trimOffspring"),sQuery(id+"F0.wireOp",EDGE,"E5.filletArc"),sQuery(id+"F0.wireOp",EDGE,"E6.filletArc"),sQuery(id+"F0.wireOp",EDGE,"E7.1.0"),sQuery(id+"F0.wireOp",EDGE,"E7.1.1"),sQuery(id+"F0.wireOp",EDGE,"E7.1.2"),sQuery(id+"F0.wireOp",EDGE,"E7.1.3"),sQuery(id+"F0.wireOp",EDGE,"E7.1.4"),sQuery(id+"F0.wireOp",EDGE,"E7.1.5"),sQuery(id+"F0.wireOp",EDGE,"E7.1.6"),sQuery(id+"F0.wireOp",EDGE,"E7.2.0"),sQuery(id+"F0.wireOp",EDGE,"E7.2.1"),sQuery(id+"F0.wireOp",EDGE,"E7.2.2"),sQuery(id+"F0.wireOp",EDGE,"E7.2.3"),sQuery(id+"F0.wireOp",EDGE,"E7.2.4"),sQuery(id+"F0.wireOp",EDGE,"E7.2.5"),sQuery(id+"F0.wireOp",EDGE,"E7.2.6"),sQuery(id+"F0.wireOp",EDGE,"E7.3.0"),sQuery(id+"F0.wireOp",EDGE,"E7.3.1"),sQuery(id+"F0.wireOp",EDGE,"E7.3.2"),sQuery(id+"F0.wireOp",EDGE,"E7.3.3"),sQuery(id+"F0.wireOp",EDGE,"E7.3.4"),sQuery(id+"F0.wireOp",EDGE,"E7.3.5"),sQuery(id+"F0.wireOp",EDGE,"E7.3.6"),sQuery(id+"F0.wireOp",EDGE,"E7.4.0"),sQuery(id+"F0.wireOp",EDGE,"E7.4.1"),sQuery(id+"F0.wireOp",EDGE,"E7.4.2"),sQuery(id+"F0.wireOp",EDGE,"E7.4.3"),sQuery(id+"F0.wireOp",EDGE,"E7.4.4"),sQuery(id+"F0.wireOp",EDGE,"E7.4.5"),sQuery(id+"F0.wireOp",EDGE,"E7.4.6"),sQuery(id+"F0.wireOp",EDGE,"E7.5.0"),sQuery(id+"F0.wireOp",EDGE,"E7.5.1"),sQuery(id+"F0.wireOp",EDGE,"E7.5.2"),sQuery(id+"F0.wireOp",EDGE,"E7.5.3"),sQuery(id+"F0.wireOp",EDGE,"E7.5.4"),sQuery(id+"F0.wireOp",EDGE,"E7.5.5"),sQuery(id+"F0.wireOp",EDGE,"E7.5.6"),sQuery(id+"F0.wireOp",EDGE,"E7.6.0"),sQuery(id+"F0.wireOp",EDGE,"E7.6.1"),sQuery(id+"F0.wireOp",EDGE,"E7.6.2"),sQuery(id+"F0.wireOp",EDGE,"E7.6.3"),sQuery(id+"F0.wireOp",EDGE,"E7.6.4"),sQuery(id+"F0.wireOp",EDGE,"E7.6.5"),sQuery(id+"F0.wireOp",EDGE,"E7.6.6"),sQuery(id+"F0.wireOp",EDGE,"E7.7.0"),sQuery(id+"F0.wireOp",EDGE,"E7.7.1"),sQuery(id+"F0.wireOp",EDGE,"E7.7.2"),sQuery(id+"F0.wireOp",EDGE,"E7.7.3"),sQuery(id+"F0.wireOp",EDGE,"E7.7.4"),sQuery(id+"F0.wireOp",EDGE,"E7.7.5"),sQuery(id+"F0.wireOp",EDGE,"E7.7.6"),sQuery(id+"F0.wireOp",EDGE,"E7.8.0"),sQuery(id+"F0.wireOp",EDGE,"E7.8.1"),sQuery(id+"F0.wireOp",EDGE,"E7.8.2"),sQuery(id+"F0.wireOp",EDGE,"E7.8.3"),sQuery(id+"F0.wireOp",EDGE,"E7.8.4"),sQuery(id+"F0.wireOp",EDGE,"E7.8.5"),sQuery(id+"F0.wireOp",EDGE,"E7.8.6"),sQuery(id+"F0.wireOp",EDGE,"E7.9.0"),sQuery(id+"F0.wireOp",EDGE,"E7.9.1"),sQuery(id+"F0.wireOp",EDGE,"E7.9.2"),sQuery(id+"F0.wireOp",EDGE,"E7.9.3"),sQuery(id+"F0.wireOp",EDGE,"E7.9.4"),sQuery(id+"F0.wireOp",EDGE,"E7.9.5"),sQuery(id+"F0.wireOp",EDGE,"E7.9.6"),sQuery(id+"F0.wireOp",EDGE,"E7.10.0"),sQuery(id+"F0.wireOp",EDGE,"E7.10.1"),sQuery(id+"F0.wireOp",EDGE,"E7.10.2"),sQuery(id+"F0.wireOp",EDGE,"E7.10.3"),sQuery(id+"F0.wireOp",EDGE,"E7.10.4"),sQuery(id+"F0.wireOp",EDGE,"E7.10.5"),sQuery(id+"F0.wireOp",EDGE,"E7.10.6"),sQuery(id+"F0.wireOp",EDGE,"E7.11.0"),sQuery(id+"F0.wireOp",EDGE,"E7.11.1"),sQuery(id+"F0.wireOp",EDGE,"E7.11.2"),sQuery(id+"F0.wireOp",EDGE,"E7.11.3"),sQuery(id+"F0.wireOp",EDGE,"E7.11.4"),sQuery(id+"F0.wireOp",EDGE,"E7.11.5"),sQuery(id+"F0.wireOp",EDGE,"E7.11.6"),sQuery(id+"F0.wireOp",EDGE,"E7.12.0"),sQuery(id+"F0.wireOp",EDGE,"E7.12.1"),sQuery(id+"F0.wireOp",EDGE,"E7.12.2"),sQuery(id+"F0.wireOp",EDGE,"E7.12.3"),sQuery(id+"F0.wireOp",EDGE,"E7.12.4"),sQuery(id+"F0.wireOp",EDGE,"E7.12.5"),sQuery(id+"F0.wireOp",EDGE,"E7.12.6"),sQuery(id+"F0.wireOp",EDGE,"E7.13.0"),sQuery(id+"F0.wireOp",EDGE,"E7.13.1"),sQuery(id+"F0.wireOp",EDGE,"E7.13.2"),sQuery(id+"F0.wireOp",EDGE,"E7.13.3"),sQuery(id+"F0.wireOp",EDGE,"E7.13.4"),sQuery(id+"F0.wireOp",EDGE,"E7.13.5"),sQuery(id+"F0.wireOp",EDGE,"E7.13.6"),sQuery(id+"F0.wireOp",EDGE,"E7.14.0"),sQuery(id+"F0.wireOp",EDGE,"E7.14.1"),sQuery(id+"F0.wireOp",EDGE,"E7.14.2"),sQuery(id+"F0.wireOp",EDGE,"E7.14.3"),sQuery(id+"F0.wireOp",EDGE,"E7.14.4"),sQuery(id+"F0.wireOp",EDGE,"E7.14.5"),sQuery(id+"F0.wireOp",EDGE,"E7.14.6"),sQuery(id+"F0.wireOp",EDGE,"E7.15.0"),sQuery(id+"F0.wireOp",EDGE,"E7.15.1"),sQuery(id+"F0.wireOp",EDGE,"E7.15.2"),sQuery(id+"F0.wireOp",EDGE,"E7.15.3"),sQuery(id+"F0.wireOp",EDGE,"E7.15.4"),sQuery(id+"F0.wireOp",EDGE,"E7.15.5"),sQuery(id+"F0.wireOp",EDGE,"E7.15.6"),sQuery(id+"F0.wireOp",EDGE,"E7.16.0"),sQuery(id+"F0.wireOp",EDGE,"E7.16.1"),sQuery(id+"F0.wireOp",EDGE,"E7.16.2"),sQuery(id+"F0.wireOp",EDGE,"E7.16.3"),sQuery(id+"F0.wireOp",EDGE,"E7.16.4"),sQuery(id+"F0.wireOp",EDGE,"E7.16.5"),sQuery(id+"F0.wireOp",EDGE,"E7.16.6"),sQuery(id+"F0.wireOp",EDGE,"E7.17.0"),sQuery(id+"F0.wireOp",EDGE,"E7.17.1"),sQuery(id+"F0.wireOp",EDGE,"E7.17.2"),sQuery(id+"F0.wireOp",EDGE,"E7.17.3"),sQuery(id+"F0.wireOp",EDGE,"E7.17.4"),sQuery(id+"F0.wireOp",EDGE,"E7.17.5"),sQuery(id+"F0.wireOp",EDGE,"E7.17.6"),sQuery(id+"F0.wireOp",EDGE,"E7.18.0"),sQuery(id+"F0.wireOp",EDGE,"E7.18.1"),sQuery(id+"F0.wireOp",EDGE,"E7.18.2"),sQuery(id+"F0.wireOp",EDGE,"E7.18.3"),sQuery(id+"F0.wireOp",EDGE,"E7.18.4"),sQuery(id+"F0.wireOp",EDGE,"E7.18.5"),sQuery(id+"F0.wireOp",EDGE,"E7.18.6"),sQuery(id+"F0.wireOp",EDGE,"E7.19.0"),sQuery(id+"F0.wireOp",EDGE,"E7.19.1"),sQuery(id+"F0.wireOp",EDGE,"E7.19.2"),sQuery(id+"F0.wireOp",EDGE,"E7.19.3"),sQuery(id+"F0.wireOp",EDGE,"E7.19.4"),sQuery(id+"F0.wireOp",EDGE,"E7.19.5"),sQuery(id+"F0.wireOp",EDGE,"E7.19.6"),sQuery(id+"F0.wireOp",EDGE,"E7.20.0"),sQuery(id+"F0.wireOp",EDGE,"E7.20.1"),sQuery(id+"F0.wireOp",EDGE,"E7.20.2"),sQuery(id+"F0.wireOp",EDGE,"E7.20.3"),sQuery(id+"F0.wireOp",EDGE,"E7.20.4"),sQuery(id+"F0.wireOp",EDGE,"E7.20.5"),sQuery(id+"F0.wireOp",EDGE,"E7.20.6"),sQuery(id+"F0.wireOp",EDGE,"E7.21.0"),sQuery(id+"F0.wireOp",EDGE,"E7.21.1"),sQuery(id+"F0.wireOp",EDGE,"E7.21.2"),sQuery(id+"F0.wireOp",EDGE,"E7.21.3"),sQuery(id+"F0.wireOp",EDGE,"E7.21.4"),sQuery(id+"F0.wireOp",EDGE,"E7.21.5"),sQuery(id+"F0.wireOp",EDGE,"E7.21.6"),sQuery(id+"F0.wireOp",EDGE,"E7.22.0"),sQuery(id+"F0.wireOp",EDGE,"E7.22.1"),sQuery(id+"F0.wireOp",EDGE,"E7.22.2"),sQuery(id+"F0.wireOp",EDGE,"E7.22.3"),sQuery(id+"F0.wireOp",EDGE,"E7.22.4"),sQuery(id+"F0.wireOp",EDGE,"E7.22.5"),sQuery(id+"F0.wireOp",EDGE,"E7.22.6"),sQuery(id+"F0.wireOp",EDGE,"E7.23.0"),sQuery(id+"F0.wireOp",EDGE,"E7.23.1"),sQuery(id+"F0.wireOp",EDGE,"E7.23.2"),sQuery(id+"F0.wireOp",EDGE,"E7.23.3"),sQuery(id+"F0.wireOp",EDGE,"E7.23.4"),sQuery(id+"F0.wireOp",EDGE,"E7.23.5"),sQuery(id+"F0.wireOp",EDGE,"E7.23.6"),sQuery(id+"F0.wireOp",EDGE,"E7.24.0"),sQuery(id+"F0.wireOp",EDGE,"E7.24.1"),sQuery(id+"F0.wireOp",EDGE,"E7.24.2"),sQuery(id+"F0.wireOp",EDGE,"E7.24.3"),sQuery(id+"F0.wireOp",EDGE,"E7.24.4"),sQuery(id+"F0.wireOp",EDGE,"E7.24.5"),sQuery(id+"F0.wireOp",EDGE,"E7.24.6"),sQuery(id+"F0.wireOp",EDGE,"E7.25.0"),sQuery(id+"F0.wireOp",EDGE,"E7.25.1"),sQuery(id+"F0.wireOp",EDGE,"E7.25.2"),sQuery(id+"F0.wireOp",EDGE,"E7.25.3"),sQuery(id+"F0.wireOp",EDGE,"E7.25.4"),sQuery(id+"F0.wireOp",EDGE,"E7.25.5"),sQuery(id+"F0.wireOp",EDGE,"E7.25.6"),sQuery(id+"F0.wireOp",EDGE,"E7.26.0"),sQuery(id+"F0.wireOp",EDGE,"E7.26.1"),sQuery(id+"F0.wireOp",EDGE,"E7.26.2"),sQuery(id+"F0.wireOp",EDGE,"E7.26.3"),sQuery(id+"F0.wireOp",EDGE,"E7.26.4"),sQuery(id+"F0.wireOp",EDGE,"E7.26.5"),sQuery(id+"F0.wireOp",EDGE,"E7.26.6"),sQuery(id+"F0.wireOp",EDGE,"E7.27.0"),sQuery(id+"F0.wireOp",EDGE,"E7.27.1"),sQuery(id+"F0.wireOp",EDGE,"E7.27.2"),sQuery(id+"F0.wireOp",EDGE,"E7.27.3"),sQuery(id+"F0.wireOp",EDGE,"E7.27.4"),sQuery(id+"F0.wireOp",EDGE,"E7.27.5"),sQuery(id+"F0.wireOp",EDGE,"E7.27.6"),sQuery(id+"F0.wireOp",EDGE,"E7.28.0"),sQuery(id+"F0.wireOp",EDGE,"E7.28.1"),sQuery(id+"F0.wireOp",EDGE,"E7.28.2"),sQuery(id+"F0.wireOp",EDGE,"E7.28.3"),sQuery(id+"F0.wireOp",EDGE,"E7.28.4"),sQuery(id+"F0.wireOp",EDGE,"E7.28.5"),sQuery(id+"F0.wireOp",EDGE,"E7.28.6"),sQuery(id+"F0.wireOp",EDGE,"E7.29.0"),sQuery(id+"F0.wireOp",EDGE,"E7.29.1"),sQuery(id+"F0.wireOp",EDGE,"E7.29.2"),sQuery(id+"F0.wireOp",EDGE,"E7.29.3"),sQuery(id+"F0.wireOp",EDGE,"E7.29.4"),sQuery(id+"F0.wireOp",EDGE,"E7.29.5"),sQuery(id+"F0.wireOp",EDGE,"E7.29.6"),sQuery(id+"F0.wireOp",EDGE,"E7.30.0"),sQuery(id+"F0.wireOp",EDGE,"E7.30.1"),sQuery(id+"F0.wireOp",EDGE,"E7.30.2"),sQuery(id+"F0.wireOp",EDGE,"E7.30.3"),sQuery(id+"F0.wireOp",EDGE,"E7.30.4"),sQuery(id+"F0.wireOp",EDGE,"E7.30.5"),sQuery(id+"F0.wireOp",EDGE,"E7.30.6"),sQuery(id+"F0.wireOp",EDGE,"E7.31.0"),sQuery(id+"F0.wireOp",EDGE,"E7.31.1"),sQuery(id+"F0.wireOp",EDGE,"E7.31.2"),sQuery(id+"F0.wireOp",EDGE,"E7.31.3"),sQuery(id+"F0.wireOp",EDGE,"E7.31.4"),sQuery(id+"F0.wireOp",EDGE,"E7.31.5"),sQuery(id+"F0.wireOp",EDGE,"E7.31.6"),sQuery(id+"F0.wireOp",EDGE,"E7.32.0"),sQuery(id+"F0.wireOp",EDGE,"E7.32.1"),sQuery(id+"F0.wireOp",EDGE,"E7.32.2"),sQuery(id+"F0.wireOp",EDGE,"E7.32.3"),sQuery(id+"F0.wireOp",EDGE,"E7.32.4"),sQuery(id+"F0.wireOp",EDGE,"E7.32.5"),sQuery(id+"F0.wireOp",EDGE,"E7.32.6"),sQuery(id+"F0.wireOp",EDGE,"E7.33.0"),sQuery(id+"F0.wireOp",EDGE,"E7.33.1"),sQuery(id+"F0.wireOp",EDGE,"E7.33.2"),sQuery(id+"F0.wireOp",EDGE,"E7.33.3"),sQuery(id+"F0.wireOp",EDGE,"E7.33.4"),sQuery(id+"F0.wireOp",EDGE,"E7.33.5"),sQuery(id+"F0.wireOp",EDGE,"E7.33.6"),sQuery(id+"F0.wireOp",EDGE,"E7.34.0"),sQuery(id+"F0.wireOp",EDGE,"E7.34.1"),sQuery(id+"F0.wireOp",EDGE,"E7.34.2"),sQuery(id+"F0.wireOp",EDGE,"E7.34.3"),sQuery(id+"F0.wireOp",EDGE,"E7.34.4"),sQuery(id+"F0.wireOp",EDGE,"E7.34.5"),sQuery(id+"F0.wireOp",EDGE,"E7.34.6"),sQuery(id+"F0.wireOp",EDGE,"E7.35.0"),sQuery(id+"F0.wireOp",EDGE,"E7.35.1"),sQuery(id+"F0.wireOp",EDGE,"E7.35.2"),sQuery(id+"F0.wireOp",EDGE,"E7.35.3"),sQuery(id+"F0.wireOp",EDGE,"E7.35.4"),sQuery(id+"F0.wireOp",EDGE,"E7.35.5"),sQuery(id+"F0.wireOp",EDGE,"E7.35.6"),sQuery(id+"F0.wireOp",EDGE,"E7.36.0"),sQuery(id+"F0.wireOp",EDGE,"E7.36.1"),sQuery(id+"F0.wireOp",EDGE,"E7.36.2"),sQuery(id+"F0.wireOp",EDGE,"E7.36.3"),sQuery(id+"F0.wireOp",EDGE,"E7.36.4"),sQuery(id+"F0.wireOp",EDGE,"E7.36.5"),sQuery(id+"F0.wireOp",EDGE,"E7.36.6"),sQuery(id+"F0.wireOp",EDGE,"E7.37.0"),sQuery(id+"F0.wireOp",EDGE,"E7.37.1"),sQuery(id+"F0.wireOp",EDGE,"E7.37.2"),sQuery(id+"F0.wireOp",EDGE,"E7.37.3"),sQuery(id+"F0.wireOp",EDGE,"E7.37.4"),sQuery(id+"F0.wireOp",EDGE,"E7.37.5"),sQuery(id+"F0.wireOp",EDGE,"E7.37.6"),sQuery(id+"F0.wireOp",EDGE,"E7.38.0"),sQuery(id+"F0.wireOp",EDGE,"E7.38.1"),sQuery(id+"F0.wireOp",EDGE,"E7.38.2"),sQuery(id+"F0.wireOp",EDGE,"E7.38.3"),sQuery(id+"F0.wireOp",EDGE,"E7.38.4"),sQuery(id+"F0.wireOp",EDGE,"E7.38.5"),sQuery(id+"F0.wireOp",EDGE,"E7.38.6"),sQuery(id+"F0.wireOp",EDGE,"E7.39.0"),sQuery(id+"F0.wireOp",EDGE,"E7.39.1"),sQuery(id+"F0.wireOp",EDGE,"E7.39.2"),sQuery(id+"F0.wireOp",EDGE,"E7.39.3"),sQuery(id+"F0.wireOp",EDGE,"E7.39.4"),sQuery(id+"F0.wireOp",EDGE,"E7.39.5"),sQuery(id+"F0.wireOp",EDGE,"E7.39.6"),sQuery(id+"F0.wireOp",EDGE,"E7.40.0"),sQuery(id+"F0.wireOp",EDGE,"E7.40.1"),sQuery(id+"F0.wireOp",EDGE,"E7.40.2"),sQuery(id+"F0.wireOp",EDGE,"E7.40.3"),sQuery(id+"F0.wireOp",EDGE,"E7.40.4"),sQuery(id+"F0.wireOp",EDGE,"E7.40.5"),sQuery(id+"F0.wireOp",EDGE,"E7.40.6"),sQuery(id+"F0.wireOp",EDGE,"E7.41.0"),sQuery(id+"F0.wireOp",EDGE,"E7.41.1"),sQuery(id+"F0.wireOp",EDGE,"E7.41.2"),sQuery(id+"F0.wireOp",EDGE,"E7.41.3"),sQuery(id+"F0.wireOp",EDGE,"E7.41.4"),sQuery(id+"F0.wireOp",EDGE,"E7.41.5"),sQuery(id+"F0.wireOp",EDGE,"E7.41.6"),sQuery(id+"F0.wireOp",EDGE,"E7.42.0"),sQuery(id+"F0.wireOp",EDGE,"E7.42.1"),sQuery(id+"F0.wireOp",EDGE,"E7.42.2"),sQuery(id+"F0.wireOp",EDGE,"E7.42.3"),sQuery(id+"F0.wireOp",EDGE,"E7.42.4"),sQuery(id+"F0.wireOp",EDGE,"E7.42.5"),sQuery(id+"F0.wireOp",EDGE,"E7.42.6"),sQuery(id+"F0.wireOp",EDGE,"E7.43.0"),sQuery(id+"F0.wireOp",EDGE,"E7.43.1"),sQuery(id+"F0.wireOp",EDGE,"E7.43.2"),sQuery(id+"F0.wireOp",EDGE,"E7.43.3"),sQuery(id+"F0.wireOp",EDGE,"E7.43.4"),sQuery(id+"F0.wireOp",EDGE,"E7.43.5"),sQuery(id+"F0.wireOp",EDGE,"E7.43.6"),sQuery(id+"F0.wireOp",EDGE,"E7.44.0"),sQuery(id+"F0.wireOp",EDGE,"E7.44.1"),sQuery(id+"F0.wireOp",EDGE,"E7.44.2"),sQuery(id+"F0.wireOp",EDGE,"E7.44.3"),sQuery(id+"F0.wireOp",EDGE,"E7.44.4"),sQuery(id+"F0.wireOp",EDGE,"E7.44.5"),sQuery(id+"F0.wireOp",EDGE,"E7.44.6"),sQuery(id+"F0.wireOp",EDGE,"E7.45.0"),sQuery(id+"F0.wireOp",EDGE,"E7.45.1"),sQuery(id+"F0.wireOp",EDGE,"E7.45.2"),sQuery(id+"F0.wireOp",EDGE,"E7.45.3"),sQuery(id+"F0.wireOp",EDGE,"E7.45.4"),sQuery(id+"F0.wireOp",EDGE,"E7.45.5"),sQuery(id+"F0.wireOp",EDGE,"E7.45.6"),sQuery(id+"F0.wireOp",EDGE,"E7.46.0"),sQuery(id+"F0.wireOp",EDGE,"E7.46.1"),sQuery(id+"F0.wireOp",EDGE,"E7.46.2"),sQuery(id+"F0.wireOp",EDGE,"E7.46.3"),sQuery(id+"F0.wireOp",EDGE,"E7.46.4"),sQuery(id+"F0.wireOp",EDGE,"E7.46.5"),sQuery(id+"F0.wireOp",EDGE,"E7.46.6"),sQuery(id+"F0.wireOp",EDGE,"E7.47.0"),sQuery(id+"F0.wireOp",EDGE,"E7.47.1"),sQuery(id+"F0.wireOp",EDGE,"E7.47.2"),sQuery(id+"F0.wireOp",EDGE,"E7.47.3"),sQuery(id+"F0.wireOp",EDGE,"E7.47.4"),sQuery(id+"F0.wireOp",EDGE,"E7.47.5"),sQuery(id+"F0.wireOp",EDGE,"E7.47.6"),sQuery(id+"F0.wireOp",EDGE,"E7.48.0"),sQuery(id+"F0.wireOp",EDGE,"E7.48.1"),sQuery(id+"F0.wireOp",EDGE,"E7.48.2"),sQuery(id+"F0.wireOp",EDGE,"E7.48.3"),sQuery(id+"F0.wireOp",EDGE,"E7.48.4"),sQuery(id+"F0.wireOp",EDGE,"E7.48.5"),sQuery(id+"F0.wireOp",EDGE,"E7.48.6"),sQuery(id+"F0.wireOp",EDGE,"E7.49.0"),sQuery(id+"F0.wireOp",EDGE,"E7.49.1"),sQuery(id+"F0.wireOp",EDGE,"E7.49.2"),sQuery(id+"F0.wireOp",EDGE,"E7.49.3"),sQuery(id+"F0.wireOp",EDGE,"E7.49.4"),sQuery(id+"F0.wireOp",EDGE,"E7.49.5"),sQuery(id+"F0.wireOp",EDGE,"E7.49.6"),sQuery(id+"F0.wireOp",EDGE,"E7.50.0"),sQuery(id+"F0.wireOp",EDGE,"E7.50.1"),sQuery(id+"F0.wireOp",EDGE,"E7.50.2"),sQuery(id+"F0.wireOp",EDGE,"E7.50.3"),sQuery(id+"F0.wireOp",EDGE,"E7.50.4"),sQuery(id+"F0.wireOp",EDGE,"E7.50.5"),sQuery(id+"F0.wireOp",EDGE,"E7.50.6"),sQuery(id+"F0.wireOp",EDGE,"E7.51.0"),sQuery(id+"F0.wireOp",EDGE,"E7.51.1"),sQuery(id+"F0.wireOp",EDGE,"E7.51.2"),sQuery(id+"F0.wireOp",EDGE,"E7.51.3"),sQuery(id+"F0.wireOp",EDGE,"E7.51.4"),sQuery(id+"F0.wireOp",EDGE,"E7.51.5"),sQuery(id+"F0.wireOp",EDGE,"E7.51.6"),sQuery(id+"F0.wireOp",EDGE,"E7.52.0"),sQuery(id+"F0.wireOp",EDGE,"E7.52.1"),sQuery(id+"F0.wireOp",EDGE,"E7.52.2"),sQuery(id+"F0.wireOp",EDGE,"E7.52.3"),sQuery(id+"F0.wireOp",EDGE,"E7.52.4"),sQuery(id+"F0.wireOp",EDGE,"E7.52.5"),sQuery(id+"F0.wireOp",EDGE,"E7.52.6"),sQuery(id+"F0.wireOp",EDGE,"E7.53.0"),sQuery(id+"F0.wireOp",EDGE,"E7.53.1"),sQuery(id+"F0.wireOp",EDGE,"E7.53.2"),sQuery(id+"F0.wireOp",EDGE,"E7.53.3"),sQuery(id+"F0.wireOp",EDGE,"E7.53.4"),sQuery(id+"F0.wireOp",EDGE,"E7.53.5"),sQuery(id+"F0.wireOp",EDGE,"E7.53.6"),sQuery(id+"F0.wireOp",EDGE,"E7.54.0"),sQuery(id+"F0.wireOp",EDGE,"E7.54.1"),sQuery(id+"F0.wireOp",EDGE,"E7.54.2"),sQuery(id+"F0.wireOp",EDGE,"E7.54.3"),sQuery(id+"F0.wireOp",EDGE,"E7.54.4"),sQuery(id+"F0.wireOp",EDGE,"E7.54.5"),sQuery(id+"F0.wireOp",EDGE,"E7.54.6"),sQuery(id+"F0.wireOp",EDGE,"E7.55.0"),sQuery(id+"F0.wireOp",EDGE,"E7.55.1"),sQuery(id+"F0.wireOp",EDGE,"E7.55.2"),sQuery(id+"F0.wireOp",EDGE,"E7.55.3"),sQuery(id+"F0.wireOp",EDGE,"E7.55.4"),sQuery(id+"F0.wireOp",EDGE,"E7.55.5"),sQuery(id+"F0.wireOp",EDGE,"E7.55.6"),sQuery(id+"F0.wireOp",EDGE,"E7.56.0"),sQuery(id+"F0.wireOp",EDGE,"E7.56.1"),sQuery(id+"F0.wireOp",EDGE,"E7.56.2"),sQuery(id+"F0.wireOp",EDGE,"E7.56.3"),sQuery(id+"F0.wireOp",EDGE,"E7.56.4"),sQuery(id+"F0.wireOp",EDGE,"E7.56.5"),sQuery(id+"F0.wireOp",EDGE,"E7.56.6"),sQuery(id+"F0.wireOp",EDGE,"E7.57.0"),sQuery(id+"F0.wireOp",EDGE,"E7.57.1"),sQuery(id+"F0.wireOp",EDGE,"E7.57.2"),sQuery(id+"F0.wireOp",EDGE,"E7.57.3"),sQuery(id+"F0.wireOp",EDGE,"E7.57.4"),sQuery(id+"F0.wireOp",EDGE,"E7.57.5"),sQuery(id+"F0.wireOp",EDGE,"E7.57.6"),sQuery(id+"F0.wireOp",EDGE,"E7.58.0"),sQuery(id+"F0.wireOp",EDGE,"E7.58.1"),sQuery(id+"F0.wireOp",EDGE,"E7.58.2"),sQuery(id+"F0.wireOp",EDGE,"E7.58.3"),sQuery(id+"F0.wireOp",EDGE,"E7.58.4"),sQuery(id+"F0.wireOp",EDGE,"E7.58.5"),sQuery(id+"F0.wireOp",EDGE,"E7.58.6"),sQuery(id+"F0.wireOp",EDGE,"E7.59.0"),sQuery(id+"F0.wireOp",EDGE,"E7.59.1"),sQuery(id+"F0.wireOp",EDGE,"E7.59.2"),sQuery(id+"F0.wireOp",EDGE,"E7.59.3"),sQuery(id+"F0.wireOp",EDGE,"E7.59.4"),sQuery(id+"F0.wireOp",EDGE,"E7.59.5"),sQuery(id+"F0.wireOp",EDGE,"E7.59.6"),sQuery(id+"F0.wireOp",EDGE,"E7.60.0"),sQuery(id+"F0.wireOp",EDGE,"E7.60.1"),sQuery(id+"F0.wireOp",EDGE,"E7.60.2"),sQuery(id+"F0.wireOp",EDGE,"E7.60.3"),sQuery(id+"F0.wireOp",EDGE,"E7.60.4"),sQuery(id+"F0.wireOp",EDGE,"E7.60.5"),sQuery(id+"F0.wireOp",EDGE,"E7.60.6"),sQuery(id+"F0.wireOp",EDGE,"E7.61.0"),sQuery(id+"F0.wireOp",EDGE,"E7.61.1"),sQuery(id+"F0.wireOp",EDGE,"E7.61.2"),sQuery(id+"F0.wireOp",EDGE,"E7.61.3"),sQuery(id+"F0.wireOp",EDGE,"E7.61.4"),sQuery(id+"F0.wireOp",EDGE,"E7.61.5"),sQuery(id+"F0.wireOp",EDGE,"E7.61.6"),sQuery(id+"F0.wireOp",EDGE,"E7.62.0"),sQuery(id+"F0.wireOp",EDGE,"E7.62.1"),sQuery(id+"F0.wireOp",EDGE,"E7.62.2"),sQuery(id+"F0.wireOp",EDGE,"E7.62.3"),sQuery(id+"F0.wireOp",EDGE,"E7.62.4"),sQuery(id+"F0.wireOp",EDGE,"E7.62.5"),sQuery(id+"F0.wireOp",EDGE,"E7.62.6"),sQuery(id+"F0.wireOp",EDGE,"E7.63.0"),sQuery(id+"F0.wireOp",EDGE,"E7.63.1"),sQuery(id+"F0.wireOp",EDGE,"E7.63.2"),sQuery(id+"F0.wireOp",EDGE,"E7.63.3"),sQuery(id+"F0.wireOp",EDGE,"E7.63.4"),sQuery(id+"F0.wireOp",EDGE,"E7.63.5"),sQuery(id+"F0.wireOp",EDGE,"E7.63.6"),sQuery(id+"F0.wireOp",EDGE,"E7.64.0"),sQuery(id+"F0.wireOp",EDGE,"E7.64.1"),sQuery(id+"F0.wireOp",EDGE,"E7.64.2"),sQuery(id+"F0.wireOp",EDGE,"E7.64.3"),sQuery(id+"F0.wireOp",EDGE,"E7.64.4"),sQuery(id+"F0.wireOp",EDGE,"E7.64.5"),sQuery(id+"F0.wireOp",EDGE,"E7.64.6"),sQuery(id+"F0.wireOp",EDGE,"E7.65.0"),sQuery(id+"F0.wireOp",EDGE,"E7.65.1"),sQuery(id+"F0.wireOp",EDGE,"E7.65.2"),sQuery(id+"F0.wireOp",EDGE,"E7.65.3"),sQuery(id+"F0.wireOp",EDGE,"E7.65.4"),sQuery(id+"F0.wireOp",EDGE,"E7.65.5"),sQuery(id+"F0.wireOp",EDGE,"E7.65.6"),sQuery(id+"F0.wireOp",EDGE,"E7.66.0"),sQuery(id+"F0.wireOp",EDGE,"E7.66.1"),sQuery(id+"F0.wireOp",EDGE,"E7.66.2"),sQuery(id+"F0.wireOp",EDGE,"E7.66.3"),sQuery(id+"F0.wireOp",EDGE,"E7.66.4"),sQuery(id+"F0.wireOp",EDGE,"E7.66.5"),sQuery(id+"F0.wireOp",EDGE,"E7.66.6"),sQuery(id+"F0.wireOp",EDGE,"E7.67.0"),sQuery(id+"F0.wireOp",EDGE,"E7.67.1"),sQuery(id+"F0.wireOp",EDGE,"E7.67.2"),sQuery(id+"F0.wireOp",EDGE,"E7.67.3"),sQuery(id+"F0.wireOp",EDGE,"E7.67.4"),sQuery(id+"F0.wireOp",EDGE,"E7.67.5"),sQuery(id+"F0.wireOp",EDGE,"E7.67.6"),sQuery(id+"F0.wireOp",EDGE,"E7.68.0"),sQuery(id+"F0.wireOp",EDGE,"E7.68.1"),sQuery(id+"F0.wireOp",EDGE,"E7.68.2"),sQuery(id+"F0.wireOp",EDGE,"E7.68.3"),sQuery(id+"F0.wireOp",EDGE,"E7.68.4"),sQuery(id+"F0.wireOp",EDGE,"E7.68.5"),sQuery(id+"F0.wireOp",EDGE,"E7.68.6"),sQuery(id+"F0.wireOp",EDGE,"E7.69.0"),sQuery(id+"F0.wireOp",EDGE,"E7.69.1"),sQuery(id+"F0.wireOp",EDGE,"E7.69.2"),sQuery(id+"F0.wireOp",EDGE,"E7.69.3"),sQuery(id+"F0.wireOp",EDGE,"E7.69.4"),sQuery(id+"F0.wireOp",EDGE,"E7.69.5"),sQuery(id+"F0.wireOp",EDGE,"E7.69.6"),sQuery(id+"F0.wireOp",EDGE,"E7.70.0"),sQuery(id+"F0.wireOp",EDGE,"E7.70.1"),sQuery(id+"F0.wireOp",EDGE,"E7.70.2"),sQuery(id+"F0.wireOp",EDGE,"E7.70.3"),sQuery(id+"F0.wireOp",EDGE,"E7.70.4"),sQuery(id+"F0.wireOp",EDGE,"E7.70.5"),sQuery(id+"F0.wireOp",EDGE,"E7.70.6"),sQuery(id+"F0.wireOp",EDGE,"E7.71.0"),sQuery(id+"F0.wireOp",EDGE,"E7.71.1"),sQuery(id+"F0.wireOp",EDGE,"E7.71.2"),sQuery(id+"F0.wireOp",EDGE,"E7.71.3"),sQuery(id+"F0.wireOp",EDGE,"E7.71.4"),sQuery(id+"F0.wireOp",EDGE,"E7.71.5"),sQuery(id+"F0.wireOp",EDGE,"E7.71.6"),sQuery(id+"F0.wireOp",EDGE,"E7.72.0"),sQuery(id+"F0.wireOp",EDGE,"E7.72.1"),sQuery(id+"F0.wireOp",EDGE,"E7.72.2"),sQuery(id+"F0.wireOp",EDGE,"E7.72.3"),sQuery(id+"F0.wireOp",EDGE,"E7.72.4"),sQuery(id+"F0.wireOp",EDGE,"E7.72.5"),sQuery(id+"F0.wireOp",EDGE,"E7.72.6"),sQuery(id+"F0.wireOp",EDGE,"E7.73.0"),sQuery(id+"F0.wireOp",EDGE,"E7.73.1"),sQuery(id+"F0.wireOp",EDGE,"E7.73.2"),sQuery(id+"F0.wireOp",EDGE,"E7.73.3"),sQuery(id+"F0.wireOp",EDGE,"E7.73.4"),sQuery(id+"F0.wireOp",EDGE,"E7.73.5"),sQuery(id+"F0.wireOp",EDGE,"E7.73.6"),sQuery(id+"F0.wireOp",EDGE,"E7.74.0"),sQuery(id+"F0.wireOp",EDGE,"E7.74.1"),sQuery(id+"F0.wireOp",EDGE,"E7.74.2"),sQuery(id+"F0.wireOp",EDGE,"E7.74.3"),sQuery(id+"F0.wireOp",EDGE,"E7.74.4"),sQuery(id+"F0.wireOp",EDGE,"E7.74.5"),sQuery(id+"F0.wireOp",EDGE,"E7.74.6"),sQuery(id+"F0.wireOp",EDGE,"E7.75.0"),sQuery(id+"F0.wireOp",EDGE,"E7.75.1"),sQuery(id+"F0.wireOp",EDGE,"E7.75.2"),sQuery(id+"F0.wireOp",EDGE,"E7.75.3"),sQuery(id+"F0.wireOp",EDGE,"E7.75.4"),sQuery(id+"F0.wireOp",EDGE,"E7.75.5"),sQuery(id+"F0.wireOp",EDGE,"E7.75.6"),sQuery(id+"F0.wireOp",EDGE,"E7.76.0"),sQuery(id+"F0.wireOp",EDGE,"E7.76.1"),sQuery(id+"F0.wireOp",EDGE,"E7.76.2"),sQuery(id+"F0.wireOp",EDGE,"E7.76.3"),sQuery(id+"F0.wireOp",EDGE,"E7.76.4"),sQuery(id+"F0.wireOp",EDGE,"E7.76.5"),sQuery(id+"F0.wireOp",EDGE,"E7.76.6"),sQuery(id+"F0.wireOp",EDGE,"E7.77.0"),sQuery(id+"F0.wireOp",EDGE,"E7.77.1"),sQuery(id+"F0.wireOp",EDGE,"E7.77.2"),sQuery(id+"F0.wireOp",EDGE,"E7.77.3"),sQuery(id+"F0.wireOp",EDGE,"E7.77.4"),sQuery(id+"F0.wireOp",EDGE,"E7.77.5"),sQuery(id+"F0.wireOp",EDGE,"E7.77.6"),sQuery(id+"F0.wireOp",EDGE,"E7.78.0"),sQuery(id+"F0.wireOp",EDGE,"E7.78.1"),sQuery(id+"F0.wireOp",EDGE,"E7.78.2"),sQuery(id+"F0.wireOp",EDGE,"E7.78.3"),sQuery(id+"F0.wireOp",EDGE,"E7.78.4"),sQuery(id+"F0.wireOp",EDGE,"E7.78.5"),sQuery(id+"F0.wireOp",EDGE,"E7.78.6"),sQuery(id+"F0.wireOp",EDGE,"E7.79.0"),sQuery(id+"F0.wireOp",EDGE,"E7.79.1"),sQuery(id+"F0.wireOp",EDGE,"E7.79.2"),sQuery(id+"F0.wireOp",EDGE,"E7.79.3"),sQuery(id+"F0.wireOp",EDGE,"E7.79.4"),sQuery(id+"F0.wireOp",EDGE,"E7.79.5"),sQuery(id+"F0.wireOp",EDGE,"E7.79.6")])],"isStart":true});
            var sketch = newSketch(context, id + "F4", { "sketchPlane" : qUnion([Q0])});
            skCircle(sketch, "E9", {"center": v(0, 0) * mm, "radius": 19.05 * mm});
            skSolve(sketch);
        }
        {
            var Q0;
            Q0 = qSketchRegion(id + "F4", true);
            extrude(context, id + "F5", {"entities" : qUnion([Q0]), "operationType" : NewBodyOperationType.ADD, "depth" : 12.7 * mm, "offsetDistance" : 25.4 * mm});
        }
        {
            var Q0;
            Q0=makeQuery(id+"F5.opExtrude","CAP_FACE",FACE,{"disambiguationData":[OSD([sQuery(id+"F4.wireOp",EDGE,"E9")])],"isStart":false});
            var sketch = newSketch(context, id + "F6", { "sketchPlane" : qUnion([Q0])});
            skCircle(sketch, "E10.cCircle", {"center": v(0, 0) * mm, "radius": 6.1 * mm, "construction": true});
            skLineSegment(sketch, "E10.0", {"start": v(3.52, -6.1) * mm, "end": v(-3.52, -6.1) * mm});
            skLineSegment(sketch, "E10.1", {"start": v(-3.52, -6.1) * mm, "end": v(-7.04, 0) * mm});
            skLineSegment(sketch, "E10.2", {"start": v(-7.04, 0) * mm, "end": v(-3.52, 6.1) * mm});
            skLineSegment(sketch, "E10.3", {"start": v(-3.52, 6.1) * mm, "end": v(3.52, 6.1) * mm});
            skLineSegment(sketch, "E10.4", {"start": v(3.52, 6.1) * mm, "end": v(7.04, 0) * mm});
            skLineSegment(sketch, "E10.5", {"start": v(7.04, 0) * mm, "end": v(3.52, -6.1) * mm});
            skPoint(sketch, "E10.0.midPoint", {"position": v(0, -6.1) * mm});
            skSolve(sketch);
        }
        {
            var Q0;
            Q0 = qSketchRegion(id + "F6", true);
            extrude(context, id + "F7", {"entities" : qUnion([Q0]), "operationType" : NewBodyOperationType.ADD, "depth" : 6.35 * mm, "offsetDistance" : 25.4 * mm});
        }
        {
            var Q0;
            Q0=makeQuery(id+"F3.opExtrude","CAP_FACE",FACE,{"disambiguationData":[OSD([sQuery(id+"F2.wireOp",EDGE,"E8")])],"isStart":false});
            var sketch = newSketch(context, id + "F8", { "sketchPlane" : qUnion([Q0])});
            skCircle(sketch, "E11", {"center": v(0, 0) * mm, "radius": 4.89 * mm});
            skSolve(sketch);
        }
        {
            var Q0;
            Q0 = qSketchRegion(id + "F8", true);
            extrude(context, id + "F9", {"entities" : qUnion([Q0]), "operationType" : NewBodyOperationType.REMOVE, "oppositeDirection" : true, "depth" : 41.66 * mm, "offsetDistance" : 25.4 * mm});
        }
        {
            var Q0;
            Q0=makeQuery(id+"F3.opExtrude","CAP_FACE",FACE,{"disambiguationData":[OSD([sQuery(id+"F2.wireOp",EDGE,"E8")])],"isStart":false});
            var sketch = newSketch(context, id + "F10", { "sketchPlane" : qUnion([Q0])});
            skCircle(sketch, "E12", {"center": v(0, 0) * mm, "radius": 11.18 * mm});
            skSolve(sketch);
        }
        {
            var Q0;
            Q0 = qSketchRegion(id + "F10", true);
            extrude(context, id + "F11", {"entities" : qUnion([Q0]), "operationType" : NewBodyOperationType.REMOVE, "oppositeDirection" : true, "depth" : 16.5 * mm, "offsetDistance" : 25.4 * mm});
        }
    });
